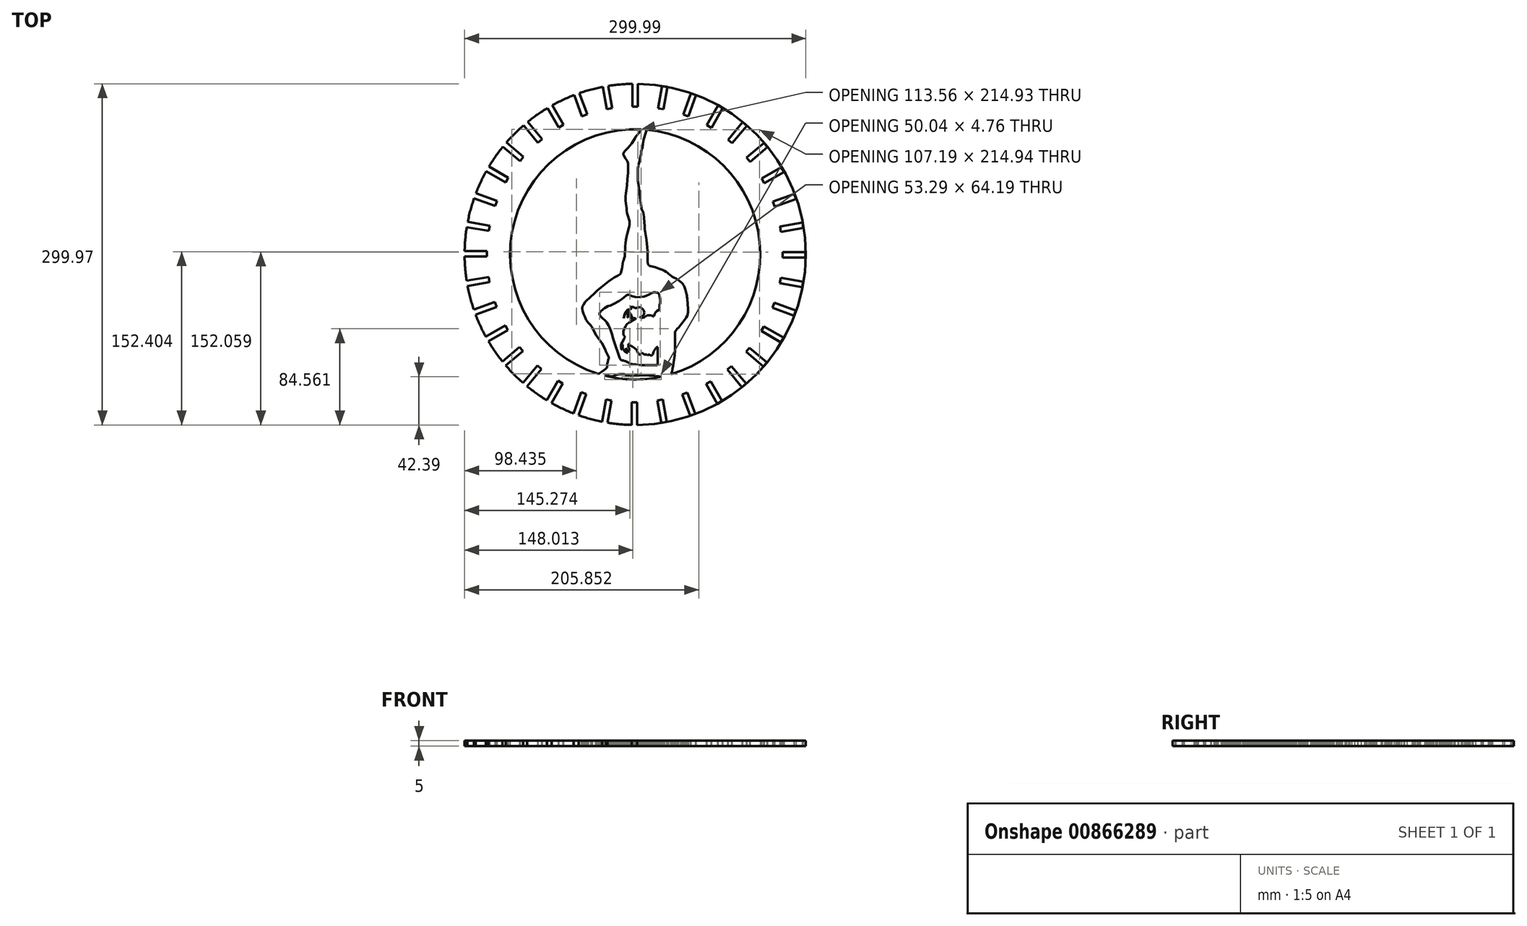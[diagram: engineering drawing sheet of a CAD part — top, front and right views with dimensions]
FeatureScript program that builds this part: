
annotation { "Feature Type Name" : "Feature", "Feature Type Description" : "" }
export const myFeature = defineFeature(function(context is Context, id is Id, definition is map)
    precondition{}
    {
        {
            var Q0;
            Q0=qCreatedBy(makeId("Top.planeOp"),FACE);
            var sketch = newSketch(context, id + "F0", { "sketchPlane" : qUnion([Q0])});
            skCircle(sketch, "E0", {"center": v(0, 0) * mm, "radius": 150 * mm});
            skLineSegment(sketch, "E1", {"start": v(0, 0) * mm, "end": v(0, 150) * mm});
            skPoint(sketch, "E2", {"position": v(0, 150) * mm});
            skPoint(sketch, "E3", {"position": v(0, 130) * mm});
            skLineSegment(sketch, "E4", {"start": v(-2.38, 130) * mm, "end": v(2.38, 130) * mm});
            skLineSegment(sketch, "E5", {"start": v(-2.38, 150) * mm, "end": v(2.37, 150) * mm});
            skLineSegment(sketch, "E6", {"start": v(-2.38, 150) * mm, "end": v(-2.38, 130) * mm});
            skLineSegment(sketch, "E7", {"start": v(2.38, 150) * mm, "end": v(2.38, 130) * mm});
            skCircle(sketch, "E8", {"center": v(0, 0) * mm, "radius": 110 * mm});
            skLineSegment(sketch, "E9.1.0", {"start": v(-28.4, 147.38) * mm, "end": v(-24.92, 127.68) * mm});
            skLineSegment(sketch, "E9.1.1", {"start": v(-23.71, 148.2) * mm, "end": v(-20.24, 128.5) * mm});
            skLineSegment(sketch, "E9.1.2", {"start": v(-28.4, 147.38) * mm, "end": v(-23.71, 148.2) * mm});
            skLineSegment(sketch, "E9.1.3", {"start": v(-24.92, 127.68) * mm, "end": v(-20.24, 128.5) * mm});
            skLineSegment(sketch, "E9.2.0", {"start": v(-53.56, 140.27) * mm, "end": v(-46.72, 121.48) * mm});
            skLineSegment(sketch, "E9.2.1", {"start": v(-49.1, 141.9) * mm, "end": v(-42.25, 123.1) * mm});
            skLineSegment(sketch, "E9.2.2", {"start": v(-53.56, 140.27) * mm, "end": v(-49.1, 141.9) * mm});
            skLineSegment(sketch, "E9.2.3", {"start": v(-46.72, 121.48) * mm, "end": v(-42.25, 123.1) * mm});
            skLineSegment(sketch, "E9.3.0", {"start": v(-77.1, 128.91) * mm, "end": v(-67.1, 111.6) * mm});
            skLineSegment(sketch, "E9.3.1", {"start": v(-73, 131.29) * mm, "end": v(-63, 113.97) * mm});
            skLineSegment(sketch, "E9.3.2", {"start": v(-77.1, 128.91) * mm, "end": v(-73, 131.29) * mm});
            skLineSegment(sketch, "E9.3.3", {"start": v(-67.1, 111.6) * mm, "end": v(-63, 113.97) * mm});
            skLineSegment(sketch, "E9.4.0", {"start": v(-98.33, 113.63) * mm, "end": v(-85.47, 98.3) * mm});
            skLineSegment(sketch, "E9.4.1", {"start": v(-94.69, 116.68) * mm, "end": v(-81.83, 101.36) * mm});
            skLineSegment(sketch, "E9.4.2", {"start": v(-98.33, 113.63) * mm, "end": v(-94.69, 116.68) * mm});
            skLineSegment(sketch, "E9.4.3", {"start": v(-85.47, 98.3) * mm, "end": v(-81.83, 101.36) * mm});
            skLineSegment(sketch, "E9.5.0", {"start": v(-116.57, 94.9) * mm, "end": v(-101.25, 82.04) * mm});
            skLineSegment(sketch, "E9.5.1", {"start": v(-113.52, 98.54) * mm, "end": v(-98.2, 85.68) * mm});
            skLineSegment(sketch, "E9.5.2", {"start": v(-116.57, 94.9) * mm, "end": v(-113.52, 98.54) * mm});
            skLineSegment(sketch, "E9.5.3", {"start": v(-101.25, 82.04) * mm, "end": v(-98.2, 85.68) * mm});
            skLineSegment(sketch, "E9.6.0", {"start": v(-131.29, 73.28) * mm, "end": v(-113.97, 63.28) * mm});
            skLineSegment(sketch, "E9.6.1", {"start": v(-128.91, 77.4) * mm, "end": v(-111.6, 67.4) * mm});
            skLineSegment(sketch, "E9.6.2", {"start": v(-131.29, 73.28) * mm, "end": v(-128.91, 77.4) * mm});
            skLineSegment(sketch, "E9.6.3", {"start": v(-113.97, 63.28) * mm, "end": v(-111.6, 67.4) * mm});
            skLineSegment(sketch, "E9.7.0", {"start": v(-142.02, 49.44) * mm, "end": v(-123.23, 42.6) * mm});
            skLineSegment(sketch, "E9.7.1", {"start": v(-140.4, 53.9) * mm, "end": v(-121.6, 47.06) * mm});
            skLineSegment(sketch, "E9.7.2", {"start": v(-142.02, 49.44) * mm, "end": v(-140.4, 53.9) * mm});
            skLineSegment(sketch, "E9.7.3", {"start": v(-123.23, 42.6) * mm, "end": v(-121.6, 47.06) * mm});
            skLineSegment(sketch, "E9.8.0", {"start": v(-148.45, 24.1) * mm, "end": v(-128.76, 20.62) * mm});
            skLineSegment(sketch, "E9.8.1", {"start": v(-147.63, 28.77) * mm, "end": v(-127.93, 25.3) * mm});
            skLineSegment(sketch, "E9.8.2", {"start": v(-148.45, 24.1) * mm, "end": v(-147.63, 28.77) * mm});
            skLineSegment(sketch, "E9.8.3", {"start": v(-128.76, 20.62) * mm, "end": v(-127.93, 25.3) * mm});
            skLineSegment(sketch, "E9.9.0", {"start": v(-150.39, -1.99) * mm, "end": v(-130.39, -1.99) * mm});
            skLineSegment(sketch, "E9.9.1", {"start": v(-150.39, 2.76) * mm, "end": v(-130.39, 2.76) * mm});
            skLineSegment(sketch, "E9.9.2", {"start": v(-150.39, -1.99) * mm, "end": v(-150.39, 2.76) * mm});
            skLineSegment(sketch, "E9.9.3", {"start": v(-130.39, -1.99) * mm, "end": v(-130.39, 2.76) * mm});
            skLineSegment(sketch, "E9.10.0", {"start": v(-147.77, -28) * mm, "end": v(-128.07, -24.53) * mm});
            skLineSegment(sketch, "E9.10.1", {"start": v(-148.59, -23.33) * mm, "end": v(-128.9, -19.85) * mm});
            skLineSegment(sketch, "E9.10.2", {"start": v(-147.77, -28) * mm, "end": v(-148.59, -23.33) * mm});
            skLineSegment(sketch, "E9.10.3", {"start": v(-128.07, -24.53) * mm, "end": v(-128.9, -19.85) * mm});
            skLineSegment(sketch, "E9.11.0", {"start": v(-140.66, -53.17) * mm, "end": v(-121.87, -46.33) * mm});
            skLineSegment(sketch, "E9.11.1", {"start": v(-142.29, -48.7) * mm, "end": v(-123.5, -41.87) * mm});
            skLineSegment(sketch, "E9.11.2", {"start": v(-140.66, -53.17) * mm, "end": v(-142.29, -48.7) * mm});
            skLineSegment(sketch, "E9.11.3", {"start": v(-121.87, -46.33) * mm, "end": v(-123.5, -41.87) * mm});
            skLineSegment(sketch, "E9.12.0", {"start": v(-129.3, -76.72) * mm, "end": v(-111.98, -66.72) * mm});
            skLineSegment(sketch, "E9.12.1", {"start": v(-131.67, -72.6) * mm, "end": v(-114.35, -62.6) * mm});
            skLineSegment(sketch, "E9.12.2", {"start": v(-129.3, -76.72) * mm, "end": v(-131.67, -72.6) * mm});
            skLineSegment(sketch, "E9.12.3", {"start": v(-111.98, -66.72) * mm, "end": v(-114.35, -62.6) * mm});
            skLineSegment(sketch, "E9.13.0", {"start": v(-114.02, -97.94) * mm, "end": v(-98.7, -85.08) * mm});
            skLineSegment(sketch, "E9.13.1", {"start": v(-117.07, -94.3) * mm, "end": v(-101.75, -81.45) * mm});
            skLineSegment(sketch, "E9.13.2", {"start": v(-114.02, -97.94) * mm, "end": v(-117.07, -94.3) * mm});
            skLineSegment(sketch, "E9.13.3", {"start": v(-98.7, -85.08) * mm, "end": v(-101.75, -81.45) * mm});
            skLineSegment(sketch, "E9.14.0", {"start": v(-95.29, -116.18) * mm, "end": v(-82.43, -100.86) * mm});
            skLineSegment(sketch, "E9.14.1", {"start": v(-98.92, -113.13) * mm, "end": v(-86.07, -97.8) * mm});
            skLineSegment(sketch, "E9.14.2", {"start": v(-95.29, -116.18) * mm, "end": v(-98.92, -113.13) * mm});
            skLineSegment(sketch, "E9.14.3", {"start": v(-82.43, -100.86) * mm, "end": v(-86.07, -97.8) * mm});
            skLineSegment(sketch, "E9.15.0", {"start": v(-73.67, -130.9) * mm, "end": v(-63.67, -113.58) * mm});
            skLineSegment(sketch, "E9.15.1", {"start": v(-77.78, -128.52) * mm, "end": v(-67.78, -111.2) * mm});
            skLineSegment(sketch, "E9.15.2", {"start": v(-73.67, -130.9) * mm, "end": v(-77.78, -128.52) * mm});
            skLineSegment(sketch, "E9.15.3", {"start": v(-63.67, -113.58) * mm, "end": v(-67.78, -111.2) * mm});
            skLineSegment(sketch, "E9.16.0", {"start": v(-49.83, -141.63) * mm, "end": v(-42.99, -122.84) * mm});
            skLineSegment(sketch, "E9.16.1", {"start": v(-54.29, -140) * mm, "end": v(-47.45, -121.21) * mm});
            skLineSegment(sketch, "E9.16.2", {"start": v(-49.83, -141.63) * mm, "end": v(-54.29, -140) * mm});
            skLineSegment(sketch, "E9.16.3", {"start": v(-42.99, -122.84) * mm, "end": v(-47.45, -121.21) * mm});
            skLineSegment(sketch, "E9.17.0", {"start": v(-24.48, -148.07) * mm, "end": v(-21, -128.37) * mm});
            skLineSegment(sketch, "E9.17.1", {"start": v(-29.16, -147.24) * mm, "end": v(-25.69, -127.55) * mm});
            skLineSegment(sketch, "E9.17.2", {"start": v(-24.48, -148.07) * mm, "end": v(-29.16, -147.24) * mm});
            skLineSegment(sketch, "E9.17.3", {"start": v(-21, -128.37) * mm, "end": v(-25.69, -127.55) * mm});
            skLineSegment(sketch, "E9.18.0", {"start": v(1.6, -150) * mm, "end": v(1.6, -130) * mm});
            skLineSegment(sketch, "E9.18.1", {"start": v(-3.15, -150) * mm, "end": v(-3.15, -130) * mm});
            skLineSegment(sketch, "E9.18.2", {"start": v(1.6, -150) * mm, "end": v(-3.15, -150) * mm});
            skLineSegment(sketch, "E9.18.3", {"start": v(1.6, -130) * mm, "end": v(-3.15, -130) * mm});
            skLineSegment(sketch, "E9.19.0", {"start": v(27.61, -147.38) * mm, "end": v(24.14, -127.68) * mm});
            skLineSegment(sketch, "E9.19.1", {"start": v(22.94, -148.2) * mm, "end": v(19.46, -128.5) * mm});
            skLineSegment(sketch, "E9.19.2", {"start": v(27.61, -147.38) * mm, "end": v(22.94, -148.2) * mm});
            skLineSegment(sketch, "E9.19.3", {"start": v(24.14, -127.68) * mm, "end": v(19.46, -128.5) * mm});
            skLineSegment(sketch, "E9.20.0", {"start": v(52.78, -140.27) * mm, "end": v(45.94, -121.48) * mm});
            skLineSegment(sketch, "E9.20.1", {"start": v(48.32, -141.9) * mm, "end": v(41.48, -123.1) * mm});
            skLineSegment(sketch, "E9.20.2", {"start": v(52.78, -140.27) * mm, "end": v(48.32, -141.9) * mm});
            skLineSegment(sketch, "E9.20.3", {"start": v(45.94, -121.48) * mm, "end": v(41.48, -123.1) * mm});
            skLineSegment(sketch, "E9.21.0", {"start": v(76.33, -128.91) * mm, "end": v(66.33, -111.6) * mm});
            skLineSegment(sketch, "E9.21.1", {"start": v(72.22, -131.29) * mm, "end": v(62.22, -113.97) * mm});
            skLineSegment(sketch, "E9.21.2", {"start": v(76.33, -128.91) * mm, "end": v(72.22, -131.29) * mm});
            skLineSegment(sketch, "E9.21.3", {"start": v(66.33, -111.6) * mm, "end": v(62.22, -113.97) * mm});
            skLineSegment(sketch, "E9.22.0", {"start": v(97.55, -113.63) * mm, "end": v(84.7, -98.3) * mm});
            skLineSegment(sketch, "E9.22.1", {"start": v(93.91, -116.68) * mm, "end": v(81.06, -101.36) * mm});
            skLineSegment(sketch, "E9.22.2", {"start": v(97.55, -113.63) * mm, "end": v(93.91, -116.68) * mm});
            skLineSegment(sketch, "E9.22.3", {"start": v(84.7, -98.3) * mm, "end": v(81.06, -101.36) * mm});
            skLineSegment(sketch, "E9.23.0", {"start": v(115.8, -94.9) * mm, "end": v(100.47, -82.04) * mm});
            skLineSegment(sketch, "E9.23.1", {"start": v(112.74, -98.54) * mm, "end": v(97.42, -85.68) * mm});
            skLineSegment(sketch, "E9.23.2", {"start": v(115.8, -94.9) * mm, "end": v(112.74, -98.54) * mm});
            skLineSegment(sketch, "E9.23.3", {"start": v(100.47, -82.04) * mm, "end": v(97.42, -85.68) * mm});
            skLineSegment(sketch, "E9.24.0", {"start": v(130.5, -73.28) * mm, "end": v(113.19, -63.28) * mm});
            skLineSegment(sketch, "E9.24.1", {"start": v(128.13, -77.4) * mm, "end": v(110.81, -67.4) * mm});
            skLineSegment(sketch, "E9.24.2", {"start": v(130.5, -73.28) * mm, "end": v(128.13, -77.4) * mm});
            skLineSegment(sketch, "E9.24.3", {"start": v(113.19, -63.28) * mm, "end": v(110.81, -67.4) * mm});
            skLineSegment(sketch, "E9.25.0", {"start": v(141.24, -49.44) * mm, "end": v(122.45, -42.6) * mm});
            skLineSegment(sketch, "E9.25.1", {"start": v(139.62, -53.9) * mm, "end": v(120.83, -47.06) * mm});
            skLineSegment(sketch, "E9.25.2", {"start": v(141.24, -49.44) * mm, "end": v(139.62, -53.9) * mm});
            skLineSegment(sketch, "E9.25.3", {"start": v(122.45, -42.6) * mm, "end": v(120.83, -47.06) * mm});
            skLineSegment(sketch, "E9.26.0", {"start": v(147.68, -24.1) * mm, "end": v(127.98, -20.62) * mm});
            skLineSegment(sketch, "E9.26.1", {"start": v(146.85, -28.77) * mm, "end": v(127.16, -25.3) * mm});
            skLineSegment(sketch, "E9.26.2", {"start": v(147.68, -24.1) * mm, "end": v(146.85, -28.77) * mm});
            skLineSegment(sketch, "E9.26.3", {"start": v(127.98, -20.62) * mm, "end": v(127.16, -25.3) * mm});
            skLineSegment(sketch, "E9.27.0", {"start": v(149.61, 1.99) * mm, "end": v(129.61, 1.99) * mm});
            skLineSegment(sketch, "E9.27.1", {"start": v(149.61, -2.76) * mm, "end": v(129.61, -2.76) * mm});
            skLineSegment(sketch, "E9.27.2", {"start": v(149.61, 1.99) * mm, "end": v(149.61, -2.76) * mm});
            skLineSegment(sketch, "E9.27.3", {"start": v(129.61, 1.99) * mm, "end": v(129.61, -2.76) * mm});
            skLineSegment(sketch, "E9.28.0", {"start": v(146.99, 28) * mm, "end": v(127.3, 24.53) * mm});
            skLineSegment(sketch, "E9.28.1", {"start": v(147.81, 23.33) * mm, "end": v(128.12, 19.85) * mm});
            skLineSegment(sketch, "E9.28.2", {"start": v(146.99, 28) * mm, "end": v(147.81, 23.33) * mm});
            skLineSegment(sketch, "E9.28.3", {"start": v(127.3, 24.53) * mm, "end": v(128.12, 19.85) * mm});
            skLineSegment(sketch, "E9.29.0", {"start": v(139.89, 53.17) * mm, "end": v(121.1, 46.33) * mm});
            skLineSegment(sketch, "E9.29.1", {"start": v(141.51, 48.7) * mm, "end": v(122.72, 41.87) * mm});
            skLineSegment(sketch, "E9.29.2", {"start": v(139.89, 53.17) * mm, "end": v(141.51, 48.7) * mm});
            skLineSegment(sketch, "E9.29.3", {"start": v(121.1, 46.33) * mm, "end": v(122.72, 41.87) * mm});
            skLineSegment(sketch, "E9.30.0", {"start": v(128.52, 76.72) * mm, "end": v(111.2, 66.72) * mm});
            skLineSegment(sketch, "E9.30.1", {"start": v(130.9, 72.6) * mm, "end": v(113.58, 62.6) * mm});
            skLineSegment(sketch, "E9.30.2", {"start": v(128.52, 76.72) * mm, "end": v(130.9, 72.6) * mm});
            skLineSegment(sketch, "E9.30.3", {"start": v(111.2, 66.72) * mm, "end": v(113.58, 62.6) * mm});
            skLineSegment(sketch, "E9.31.0", {"start": v(113.24, 97.94) * mm, "end": v(97.92, 85.08) * mm});
            skLineSegment(sketch, "E9.31.1", {"start": v(116.3, 94.3) * mm, "end": v(100.97, 81.45) * mm});
            skLineSegment(sketch, "E9.31.2", {"start": v(113.24, 97.94) * mm, "end": v(116.3, 94.3) * mm});
            skLineSegment(sketch, "E9.31.3", {"start": v(97.92, 85.08) * mm, "end": v(100.97, 81.45) * mm});
            skLineSegment(sketch, "E9.32.0", {"start": v(94.5, 116.18) * mm, "end": v(81.65, 100.86) * mm});
            skLineSegment(sketch, "E9.32.1", {"start": v(98.15, 113.13) * mm, "end": v(85.3, 97.8) * mm});
            skLineSegment(sketch, "E9.32.2", {"start": v(94.5, 116.18) * mm, "end": v(98.15, 113.13) * mm});
            skLineSegment(sketch, "E9.32.3", {"start": v(81.65, 100.86) * mm, "end": v(85.3, 97.8) * mm});
            skLineSegment(sketch, "E9.33.0", {"start": v(72.9, 130.9) * mm, "end": v(62.9, 113.58) * mm});
            skLineSegment(sketch, "E9.33.1", {"start": v(77, 128.52) * mm, "end": v(67, 111.2) * mm});
            skLineSegment(sketch, "E9.33.2", {"start": v(72.9, 130.9) * mm, "end": v(77, 128.52) * mm});
            skLineSegment(sketch, "E9.33.3", {"start": v(62.9, 113.58) * mm, "end": v(67, 111.2) * mm});
            skLineSegment(sketch, "E9.34.0", {"start": v(49.05, 141.63) * mm, "end": v(42.2, 122.84) * mm});
            skLineSegment(sketch, "E9.34.1", {"start": v(53.51, 140) * mm, "end": v(46.67, 121.21) * mm});
            skLineSegment(sketch, "E9.34.2", {"start": v(49.05, 141.63) * mm, "end": v(53.51, 140) * mm});
            skLineSegment(sketch, "E9.34.3", {"start": v(42.2, 122.84) * mm, "end": v(46.67, 121.21) * mm});
            skLineSegment(sketch, "E9.35.0", {"start": v(23.7, 148.07) * mm, "end": v(20.23, 128.37) * mm});
            skLineSegment(sketch, "E9.35.1", {"start": v(28.38, 147.24) * mm, "end": v(24.9, 127.55) * mm});
            skLineSegment(sketch, "E9.35.2", {"start": v(23.7, 148.07) * mm, "end": v(28.38, 147.24) * mm});
            skLineSegment(sketch, "E9.35.3", {"start": v(20.23, 128.37) * mm, "end": v(24.9, 127.55) * mm});
            skPoint(sketch, "E9.center", {"position": v(-0.39, 0) * mm});
            skSolve(sketch);
        }
        {
            var Q0;
            Q0=makeQuery(id+"F0.imprint","IMPRINT",FACE,{"disambiguationData":[TD([[makeQuery(id+"F0.imprint","IMPRINT",EDGE,{"derivedFrom":sQuery(id+"F0.wireOp",EDGE,"E8")}),-1.0]])]});
            extrude(context, id + "F1", {"entities" : qUnion([Q0]), "depth" : 5 * mm, "offsetDistance" : 25 * mm});
        }
        {
            var Q0;
            Q0=qCreatedBy(makeId("Top.planeOp"),FACE);
            var sketch = newSketch(context, id + "F2", { "sketchPlane" : qUnion([Q0])});
            skLineSegment(sketch, "E10", {"start": v(6.83, 111.87) * mm, "end": v(5.33, 110.02) * mm});
            skLineSegment(sketch, "E11", {"start": v(5.33, 110.02) * mm, "end": v(4.16, 108.4) * mm});
            skLineSegment(sketch, "E12", {"start": v(4.16, 108.4) * mm, "end": v(3.77, 107.3) * mm});
            skLineSegment(sketch, "E13", {"start": v(3.77, 107.3) * mm, "end": v(3.08, 106.38) * mm});
            skLineSegment(sketch, "E14", {"start": v(3.08, 106.38) * mm, "end": v(1.66, 104.89) * mm});
            skLineSegment(sketch, "E15", {"start": v(1.66, 104.89) * mm, "end": v(0.57, 103.56) * mm});
            skLineSegment(sketch, "E16", {"start": v(0.57, 103.56) * mm, "end": v(-0.34, 102.02) * mm});
            skLineSegment(sketch, "E17", {"start": v(-0.34, 102.02) * mm, "end": v(-1.86, 99.5) * mm});
            skLineSegment(sketch, "E18", {"start": v(-1.86, 99.5) * mm, "end": v(-3.07, 97.48) * mm});
            skLineSegment(sketch, "E19", {"start": v(-3.07, 97.48) * mm, "end": v(-4.65, 95.48) * mm});
            skLineSegment(sketch, "E20", {"start": v(-4.65, 95.48) * mm, "end": v(-6.3, 93.59) * mm});
            skLineSegment(sketch, "E21", {"start": v(-6.3, 93.59) * mm, "end": v(-7.83, 92.24) * mm});
            skLineSegment(sketch, "E22", {"start": v(-7.83, 92.24) * mm, "end": v(-8.94, 91.04) * mm});
            skLineSegment(sketch, "E23", {"start": v(-8.94, 91.04) * mm, "end": v(-9.48, 90.42) * mm});
            skLineSegment(sketch, "E24", {"start": v(-9.48, 90.42) * mm, "end": v(-10.02, 89.32) * mm});
            skLineSegment(sketch, "E25", {"start": v(-10.02, 89.32) * mm, "end": v(-10.24, 88.58) * mm});
            skLineSegment(sketch, "E26", {"start": v(-10.24, 88.58) * mm, "end": v(-10.37, 87.93) * mm});
            skLineSegment(sketch, "E27", {"start": v(-10.37, 87.93) * mm, "end": v(-10.37, 87.56) * mm});
            skLineSegment(sketch, "E28", {"start": v(-10.37, 87.56) * mm, "end": v(-9.88, 86.5) * mm});
            skLineSegment(sketch, "E29", {"start": v(-9.88, 86.5) * mm, "end": v(-9.17, 85.4) * mm});
            skLineSegment(sketch, "E30", {"start": v(-9.17, 85.4) * mm, "end": v(-8.4, 84.2) * mm});
            skLineSegment(sketch, "E31", {"start": v(-8.4, 84.2) * mm, "end": v(-7.39, 82.8) * mm});
            skLineSegment(sketch, "E32", {"start": v(-7.39, 82.8) * mm, "end": v(-6.91, 82.05) * mm});
            skLineSegment(sketch, "E33", {"start": v(-6.91, 82.05) * mm, "end": v(-6.5, 81.01) * mm});
            skLineSegment(sketch, "E34", {"start": v(-6.5, 81.01) * mm, "end": v(-6.3, 79.61) * mm});
            skLineSegment(sketch, "E35", {"start": v(-6.3, 79.61) * mm, "end": v(-6.2, 78.09) * mm});
            skLineSegment(sketch, "E36", {"start": v(-6.2, 78.09) * mm, "end": v(-6.28, 74.36) * mm});
            skLineSegment(sketch, "E37", {"start": v(-6.28, 74.36) * mm, "end": v(-6.4, 71.72) * mm});
            skLineSegment(sketch, "E38", {"start": v(-6.4, 71.72) * mm, "end": v(-6.74, 66.24) * mm});
            skLineSegment(sketch, "E39", {"start": v(-6.74, 66.24) * mm, "end": v(-7.25, 60.37) * mm});
            skLineSegment(sketch, "E40", {"start": v(-7.25, 60.37) * mm, "end": v(-8.18, 53.6) * mm});
            skLineSegment(sketch, "E41", {"start": v(-8.18, 53.6) * mm, "end": v(-8.44, 51.24) * mm});
            skLineSegment(sketch, "E42", {"start": v(-8.44, 51.24) * mm, "end": v(-8.5, 49.8) * mm});
            skLineSegment(sketch, "E43", {"start": v(-8.5, 49.8) * mm, "end": v(-8.34, 47.26) * mm});
            skLineSegment(sketch, "E44", {"start": v(-8.34, 47.26) * mm, "end": v(-8.04, 44.53) * mm});
            skLineSegment(sketch, "E45", {"start": v(-8.04, 44.53) * mm, "end": v(-7.56, 40.85) * mm});
            skLineSegment(sketch, "E46", {"start": v(-7.56, 40.85) * mm, "end": v(-7.37, 38.85) * mm});
            skLineSegment(sketch, "E47", {"start": v(-7.37, 38.85) * mm, "end": v(-7.07, 36.3) * mm});
            skLineSegment(sketch, "E48", {"start": v(-7.07, 36.3) * mm, "end": v(-6.66, 34.38) * mm});
            skLineSegment(sketch, "E49", {"start": v(-6.66, 34.38) * mm, "end": v(-5.65, 31.06) * mm});
            skLineSegment(sketch, "E50", {"start": v(-5.65, 31.06) * mm, "end": v(-5.3, 29.94) * mm});
            skLineSegment(sketch, "E51", {"start": v(-5.3, 29.94) * mm, "end": v(-5.12, 29.34) * mm});
            skLineSegment(sketch, "E52", {"start": v(-5.12, 29.34) * mm, "end": v(-4.98, 28.57) * mm});
            skLineSegment(sketch, "E53", {"start": v(-4.98, 28.57) * mm, "end": v(-4.91, 28) * mm});
            skLineSegment(sketch, "E54", {"start": v(-4.91, 28) * mm, "end": v(-4.91, 27.25) * mm});
            skLineSegment(sketch, "E55", {"start": v(-4.91, 27.25) * mm, "end": v(-5, 26.34) * mm});
            skLineSegment(sketch, "E56", {"start": v(-5, 26.34) * mm, "end": v(-5.41, 24.2) * mm});
            skLineSegment(sketch, "E57", {"start": v(-5.41, 24.2) * mm, "end": v(-5.59, 23.26) * mm});
            skLineSegment(sketch, "E58", {"start": v(-5.59, 23.26) * mm, "end": v(-6.96, 18.4) * mm});
            skLineSegment(sketch, "E59", {"start": v(-6.96, 18.4) * mm, "end": v(-7.52, 15.81) * mm});
            skLineSegment(sketch, "E60", {"start": v(-7.52, 15.81) * mm, "end": v(-8.04, 12.8) * mm});
            skLineSegment(sketch, "E61", {"start": v(-8.04, 12.8) * mm, "end": v(-8.43, 9.95) * mm});
            skLineSegment(sketch, "E62", {"start": v(-8.43, 9.95) * mm, "end": v(-8.64, 7.37) * mm});
            skLineSegment(sketch, "E63", {"start": v(-8.64, 7.37) * mm, "end": v(-8.9, 4.72) * mm});
            skLineSegment(sketch, "E64", {"start": v(-8.9, 4.72) * mm, "end": v(-9.08, 1.36) * mm});
            skLineSegment(sketch, "E65", {"start": v(-9.08, 1.36) * mm, "end": v(-9.08, -0.48) * mm});
            skLineSegment(sketch, "E66", {"start": v(-9.08, -0.48) * mm, "end": v(-9.08, -0.93) * mm});
            skLineSegment(sketch, "E67", {"start": v(-9.08, -0.93) * mm, "end": v(-9.18, -1.73) * mm});
            skLineSegment(sketch, "E68", {"start": v(-9.18, -1.73) * mm, "end": v(-9.63, -3.56) * mm});
            skLineSegment(sketch, "E69", {"start": v(-9.63, -3.56) * mm, "end": v(-10.14, -5) * mm});
            skLineSegment(sketch, "E70", {"start": v(-10.14, -5) * mm, "end": v(-10.54, -6.3) * mm});
            skLineSegment(sketch, "E71", {"start": v(-10.54, -6.3) * mm, "end": v(-11, -8.25) * mm});
            skLineSegment(sketch, "E72", {"start": v(-11, -8.25) * mm, "end": v(-11.46, -10.75) * mm});
            skLineSegment(sketch, "E73", {"start": v(-11.46, -10.75) * mm, "end": v(-11.77, -12.7) * mm});
            skLineSegment(sketch, "E74", {"start": v(-11.77, -12.7) * mm, "end": v(-12.11, -14.95) * mm});
            skLineSegment(sketch, "E75", {"start": v(-12.11, -14.95) * mm, "end": v(-12.45, -16.37) * mm});
            skLineSegment(sketch, "E76", {"start": v(-12.45, -16.37) * mm, "end": v(-12.62, -16.65) * mm});
            skLineSegment(sketch, "E77", {"start": v(-12.62, -16.65) * mm, "end": v(-12.95, -17.06) * mm});
            skLineSegment(sketch, "E78", {"start": v(-12.95, -17.06) * mm, "end": v(-13.17, -17.3) * mm});
            skLineSegment(sketch, "E79", {"start": v(-13.17, -17.3) * mm, "end": v(-15.1, -18.65) * mm});
            skLineSegment(sketch, "E80", {"start": v(-15.1, -18.65) * mm, "end": v(-18.23, -20.4) * mm});
            skLineSegment(sketch, "E81", {"start": v(-18.23, -20.4) * mm, "end": v(-20.15, -21.5) * mm});
            skLineSegment(sketch, "E82", {"start": v(-20.15, -21.5) * mm, "end": v(-23.4, -23.82) * mm});
            skLineSegment(sketch, "E83", {"start": v(-23.4, -23.82) * mm, "end": v(-26.73, -26.25) * mm});
            skLineSegment(sketch, "E84", {"start": v(-26.73, -26.25) * mm, "end": v(-29.8, -28.68) * mm});
            skLineSegment(sketch, "E85", {"start": v(-29.8, -28.68) * mm, "end": v(-33.17, -31.63) * mm});
            skLineSegment(sketch, "E86", {"start": v(-33.17, -31.63) * mm, "end": v(-36.23, -34.54) * mm});
            skLineSegment(sketch, "E87", {"start": v(-36.23, -34.54) * mm, "end": v(-39.37, -37.52) * mm});
            skLineSegment(sketch, "E88", {"start": v(-39.37, -37.52) * mm, "end": v(-42.95, -40.84) * mm});
            skLineSegment(sketch, "E89", {"start": v(-42.95, -40.84) * mm, "end": v(-43.82, -41.65) * mm});
            skLineSegment(sketch, "E90", {"start": v(-43.82, -41.65) * mm, "end": v(-44.03, -41.92) * mm});
            skLineSegment(sketch, "E91", {"start": v(-44.03, -41.92) * mm, "end": v(-44.92, -43.25) * mm});
            skLineSegment(sketch, "E92", {"start": v(-44.92, -43.25) * mm, "end": v(-45.46, -44.05) * mm});
            skLineSegment(sketch, "E93", {"start": v(-45.46, -44.05) * mm, "end": v(-45.77, -44.68) * mm});
            skLineSegment(sketch, "E94", {"start": v(-45.77, -44.68) * mm, "end": v(-46.1, -45.47) * mm});
            skLineSegment(sketch, "E95", {"start": v(-46.1, -45.47) * mm, "end": v(-46.27, -46) * mm});
            skLineSegment(sketch, "E96", {"start": v(-46.27, -46) * mm, "end": v(-46.4, -46.58) * mm});
            skLineSegment(sketch, "E97", {"start": v(-46.4, -46.58) * mm, "end": v(-46.48, -47.02) * mm});
            skLineSegment(sketch, "E98", {"start": v(-46.48, -47.02) * mm, "end": v(-46.53, -47.45) * mm});
            skLineSegment(sketch, "E99", {"start": v(-46.53, -47.45) * mm, "end": v(-46.55, -47.72) * mm});
            skLineSegment(sketch, "E100", {"start": v(-46.55, -47.72) * mm, "end": v(-46.54, -48.18) * mm});
            skLineSegment(sketch, "E101", {"start": v(-46.54, -48.18) * mm, "end": v(-46.4, -48.54) * mm});
            skLineSegment(sketch, "E102", {"start": v(-46.4, -48.54) * mm, "end": v(-46.32, -48.82) * mm});
            skLineSegment(sketch, "E103", {"start": v(-46.32, -48.82) * mm, "end": v(-46.22, -49.85) * mm});
            skLineSegment(sketch, "E104", {"start": v(-46.22, -49.85) * mm, "end": v(-46, -50.79) * mm});
            skLineSegment(sketch, "E105", {"start": v(-46, -50.79) * mm, "end": v(-45.26, -52.58) * mm});
            skLineSegment(sketch, "E106", {"start": v(-45.26, -52.58) * mm, "end": v(-44.28, -54.67) * mm});
            skLineSegment(sketch, "E107", {"start": v(-44.28, -54.67) * mm, "end": v(-43.34, -56.95) * mm});
            skLineSegment(sketch, "E108", {"start": v(-43.34, -56.95) * mm, "end": v(-43.06, -57.6) * mm});
            skLineSegment(sketch, "E109", {"start": v(-43.06, -57.6) * mm, "end": v(-42.4, -58.69) * mm});
            skLineSegment(sketch, "E110", {"start": v(-42.4, -58.69) * mm, "end": v(-41.05, -60.29) * mm});
            skLineSegment(sketch, "E111", {"start": v(-41.05, -60.29) * mm, "end": v(-40, -61.41) * mm});
            skLineSegment(sketch, "E112", {"start": v(-40, -61.41) * mm, "end": v(-39.2, -62.28) * mm});
            skLineSegment(sketch, "E113", {"start": v(-39.2, -62.28) * mm, "end": v(-38.64, -63.07) * mm});
            skLineSegment(sketch, "E114", {"start": v(-38.64, -63.07) * mm, "end": v(-37.84, -64.45) * mm});
            skLineSegment(sketch, "E115", {"start": v(-37.84, -64.45) * mm, "end": v(-36.99, -66.04) * mm});
            skLineSegment(sketch, "E116", {"start": v(-36.99, -66.04) * mm, "end": v(-36.03, -67.87) * mm});
            skLineSegment(sketch, "E117", {"start": v(-36.03, -67.87) * mm, "end": v(-35.19, -69.45) * mm});
            skLineSegment(sketch, "E118", {"start": v(-35.19, -69.45) * mm, "end": v(-34.36, -70.9) * mm});
            skLineSegment(sketch, "E119", {"start": v(-34.36, -70.9) * mm, "end": v(-33.82, -71.78) * mm});
            skLineSegment(sketch, "E120", {"start": v(-33.82, -71.78) * mm, "end": v(-32.49, -73.57) * mm});
            skLineSegment(sketch, "E121", {"start": v(-32.49, -73.57) * mm, "end": v(-31.58, -74.76) * mm});
            skLineSegment(sketch, "E122", {"start": v(-31.58, -74.76) * mm, "end": v(-31.28, -75.2) * mm});
            skLineSegment(sketch, "E123", {"start": v(-31.28, -75.2) * mm, "end": v(-30.68, -76.05) * mm});
            skLineSegment(sketch, "E124", {"start": v(-30.68, -76.05) * mm, "end": v(-29.53, -77.82) * mm});
            skLineSegment(sketch, "E125", {"start": v(-29.53, -77.82) * mm, "end": v(-28.26, -80.02) * mm});
            skLineSegment(sketch, "E126", {"start": v(-28.26, -80.02) * mm, "end": v(-27.46, -81.54) * mm});
            skLineSegment(sketch, "E127", {"start": v(-27.46, -81.54) * mm, "end": v(-26.17, -84) * mm});
            skLineSegment(sketch, "E128", {"start": v(-26.17, -84) * mm, "end": v(-25.83, -84.73) * mm});
            skLineSegment(sketch, "E129", {"start": v(-25.83, -84.73) * mm, "end": v(-25.77, -84.93) * mm});
            skLineSegment(sketch, "E130", {"start": v(-25.77, -84.93) * mm, "end": v(-24.35, -88.07) * mm});
            skLineSegment(sketch, "E131", {"start": v(-24.35, -88.07) * mm, "end": v(-23.47, -89.97) * mm});
            skLineSegment(sketch, "E132", {"start": v(-23.47, -89.97) * mm, "end": v(-23.27, -90.4) * mm});
            skLineSegment(sketch, "E133", {"start": v(-23.27, -90.4) * mm, "end": v(-23.23, -90.56) * mm});
            skLineSegment(sketch, "E134", {"start": v(-23.23, -90.56) * mm, "end": v(-23.19, -90.82) * mm});
            skLineSegment(sketch, "E135", {"start": v(-23.19, -90.82) * mm, "end": v(-23.19, -91.25) * mm});
            skLineSegment(sketch, "E136", {"start": v(-23.19, -91.25) * mm, "end": v(-23.3, -91.85) * mm});
            skLineSegment(sketch, "E137", {"start": v(-23.3, -91.85) * mm, "end": v(-23.57, -92.63) * mm});
            skLineSegment(sketch, "E138", {"start": v(-23.57, -92.63) * mm, "end": v(-23.84, -93.2) * mm});
            skLineSegment(sketch, "E139", {"start": v(-23.84, -93.2) * mm, "end": v(-23.98, -93.71) * mm});
            skLineSegment(sketch, "E140", {"start": v(-23.98, -93.71) * mm, "end": v(-24.13, -94.4) * mm});
            skLineSegment(sketch, "E141", {"start": v(-24.13, -94.4) * mm, "end": v(-24.3, -95.05) * mm});
            skLineSegment(sketch, "E142", {"start": v(-24.3, -95.05) * mm, "end": v(-24.46, -95.78) * mm});
            skLineSegment(sketch, "E143", {"start": v(-24.46, -95.78) * mm, "end": v(-24.58, -96.36) * mm});
            skLineSegment(sketch, "E144", {"start": v(-24.58, -96.36) * mm, "end": v(-24.65, -96.86) * mm});
            skLineSegment(sketch, "E145", {"start": v(-24.65, -96.86) * mm, "end": v(-24.68, -97.12) * mm});
            skLineSegment(sketch, "E146", {"start": v(-24.68, -97.12) * mm, "end": v(-24.68, -97.53) * mm});
            skLineSegment(sketch, "E147", {"start": v(-24.68, -97.53) * mm, "end": v(-24.6, -98.08) * mm});
            skLineSegment(sketch, "E148", {"start": v(-24.6, -98.08) * mm, "end": v(-24.58, -98.59) * mm});
            skLineSegment(sketch, "E149", {"start": v(-24.58, -98.59) * mm, "end": v(-24.58, -98.93) * mm});
            skLineSegment(sketch, "E150", {"start": v(-24.58, -98.93) * mm, "end": v(-24.61, -99.09) * mm});
            skLineSegment(sketch, "E151", {"start": v(-24.61, -99.09) * mm, "end": v(-24.8, -99.39) * mm});
            skLineSegment(sketch, "E152", {"start": v(-24.8, -99.39) * mm, "end": v(-25.08, -99.76) * mm});
            skLineSegment(sketch, "E153", {"start": v(-25.08, -99.76) * mm, "end": v(-25.42, -100.08) * mm});
            skLineSegment(sketch, "E154", {"start": v(-25.42, -100.08) * mm, "end": v(-26.37, -100.97) * mm});
            skLineSegment(sketch, "E155", {"start": v(-26.37, -100.97) * mm, "end": v(-27.57, -101.89) * mm});
            skLineSegment(sketch, "E156", {"start": v(-27.57, -101.89) * mm, "end": v(-29.77, -103.38) * mm});
            skLineSegment(sketch, "E157", {"start": v(-29.77, -103.38) * mm, "end": v(-31.64, -104.6) * mm});
            skLineSegment(sketch, "E158", {"start": v(-31.64, -104.6) * mm, "end": v(-32.04, -104.78) * mm});
            skLineSegment(sketch, "E159", {"start": v(-32.04, -104.78) * mm, "end": v(-32.66, -105.06) * mm});
            skLineSegment(sketch, "E160", {"start": v(-32.66, -105.06) * mm, "end": v(-33.66, -105.37) * mm});
            skLineSegment(sketch, "E161", {"start": v(-33.66, -105.37) * mm, "end": v(-34.75, -105.7) * mm});
            skLineSegment(sketch, "E162", {"start": v(-34.75, -105.7) * mm, "end": v(-35.27, -105.86) * mm});
            skLineSegment(sketch, "E163", {"start": v(-35.27, -105.86) * mm, "end": v(-35.72, -106) * mm});
            skLineSegment(sketch, "E164", {"start": v(-35.72, -106) * mm, "end": v(-36.2, -106.07) * mm});
            skLineSegment(sketch, "E165", {"start": v(-36.2, -106.07) * mm, "end": v(-36.59, -106.18) * mm});
            skLineSegment(sketch, "E166", {"start": v(-36.59, -106.18) * mm, "end": v(-36.77, -106.27) * mm});
            skLineSegment(sketch, "E167", {"start": v(-36.77, -106.27) * mm, "end": v(-36.82, -106.35) * mm});
            skLineSegment(sketch, "E168", {"start": v(-36.82, -106.35) * mm, "end": v(-36.85, -106.5) * mm});
            skLineSegment(sketch, "E169", {"start": v(-36.85, -106.5) * mm, "end": v(-36.8, -106.67) * mm});
            skLineSegment(sketch, "E170", {"start": v(-36.8, -106.67) * mm, "end": v(-36.67, -106.86) * mm});
            skLineSegment(sketch, "E171", {"start": v(-36.67, -106.86) * mm, "end": v(-36.46, -107.02) * mm});
            skLineSegment(sketch, "E172", {"start": v(-36.46, -107.02) * mm, "end": v(-36.31, -107.07) * mm});
            skLineSegment(sketch, "E173", {"start": v(-36.31, -107.07) * mm, "end": v(-36.19, -107.1) * mm});
            skLineSegment(sketch, "E174", {"start": v(-36.19, -107.1) * mm, "end": v(-32.78, -107.1) * mm});
            skLineSegment(sketch, "E175", {"start": v(-32.78, -107.1) * mm, "end": v(-31.03, -107.1) * mm});
            skLineSegment(sketch, "E176", {"start": v(-31.03, -107.1) * mm, "end": v(-30.82, -107.06) * mm});
            skLineSegment(sketch, "E177", {"start": v(-30.82, -107.06) * mm, "end": v(-30.43, -107) * mm});
            skLineSegment(sketch, "E178", {"start": v(-30.43, -107) * mm, "end": v(-30.06, -106.95) * mm});
            skLineSegment(sketch, "E179", {"start": v(-30.06, -106.95) * mm, "end": v(-29.54, -106.87) * mm});
            skLineSegment(sketch, "E180", {"start": v(-29.54, -106.87) * mm, "end": v(-29.47, -106.86) * mm});
            skLineSegment(sketch, "E181", {"start": v(-29.47, -106.86) * mm, "end": v(-29.23, -106.86) * mm});
            skLineSegment(sketch, "E182", {"start": v(-29.23, -106.86) * mm, "end": v(-28.9, -106.86) * mm});
            skLineSegment(sketch, "E183", {"start": v(-28.9, -106.86) * mm, "end": v(-28.3, -106.83) * mm});
            skLineSegment(sketch, "E184", {"start": v(-28.3, -106.83) * mm, "end": v(-28.03, -106.74) * mm});
            skLineSegment(sketch, "E185", {"start": v(-28.03, -106.74) * mm, "end": v(-27.64, -106.69) * mm});
            skLineSegment(sketch, "E186", {"start": v(-27.64, -106.69) * mm, "end": v(-26.96, -106.63) * mm});
            skLineSegment(sketch, "E187", {"start": v(-26.96, -106.63) * mm, "end": v(-26.51, -106.6) * mm});
            skLineSegment(sketch, "E188", {"start": v(-26.51, -106.6) * mm, "end": v(-26.23, -106.57) * mm});
            skLineSegment(sketch, "E189", {"start": v(-26.23, -106.57) * mm, "end": v(-25.95, -106.55) * mm});
            skLineSegment(sketch, "E190", {"start": v(-25.95, -106.55) * mm, "end": v(-25.7, -106.55) * mm});
            skLineSegment(sketch, "E191", {"start": v(-25.7, -106.55) * mm, "end": v(-25.33, -106.57) * mm});
            skLineSegment(sketch, "E192", {"start": v(-25.33, -106.57) * mm, "end": v(-24.74, -106.63) * mm});
            skLineSegment(sketch, "E193", {"start": v(-24.74, -106.63) * mm, "end": v(-24.06, -106.77) * mm});
            skLineSegment(sketch, "E194", {"start": v(-24.06, -106.77) * mm, "end": v(-23.53, -106.95) * mm});
            skLineSegment(sketch, "E195", {"start": v(-23.53, -106.95) * mm, "end": v(-23.19, -107.07) * mm});
            skLineSegment(sketch, "E196", {"start": v(-23.19, -107.07) * mm, "end": v(-22.54, -107.2) * mm});
            skLineSegment(sketch, "E197", {"start": v(-22.54, -107.2) * mm, "end": v(-22.07, -107.3) * mm});
            skLineSegment(sketch, "E198", {"start": v(-22.07, -107.3) * mm, "end": v(-21.23, -107.3) * mm});
            skLineSegment(sketch, "E199", {"start": v(-21.23, -107.3) * mm, "end": v(-20.48, -107.3) * mm});
            skLineSegment(sketch, "E200", {"start": v(-20.48, -107.3) * mm, "end": v(-20.06, -107.27) * mm});
            skLineSegment(sketch, "E201", {"start": v(-20.06, -107.27) * mm, "end": v(-19.74, -107.17) * mm});
            skLineSegment(sketch, "E202", {"start": v(-19.74, -107.17) * mm, "end": v(-19.26, -107.1) * mm});
            skLineSegment(sketch, "E203", {"start": v(-19.26, -107.1) * mm, "end": v(-19.02, -107.02) * mm});
            skLineSegment(sketch, "E204", {"start": v(-19.02, -107.02) * mm, "end": v(-18.3, -106.74) * mm});
            skLineSegment(sketch, "E205", {"start": v(-18.3, -106.74) * mm, "end": v(-17.46, -106.38) * mm});
            skLineSegment(sketch, "E206", {"start": v(-17.46, -106.38) * mm, "end": v(-16.84, -106.1) * mm});
            skLineSegment(sketch, "E207", {"start": v(-16.84, -106.1) * mm, "end": v(-16.35, -105.87) * mm});
            skLineSegment(sketch, "E208", {"start": v(-16.35, -105.87) * mm, "end": v(-15.79, -105.7) * mm});
            skLineSegment(sketch, "E209", {"start": v(-15.79, -105.7) * mm, "end": v(-15.1, -105.53) * mm});
            skLineSegment(sketch, "E210", {"start": v(-15.1, -105.53) * mm, "end": v(-14.59, -105.45) * mm});
            skLineSegment(sketch, "E211", {"start": v(-14.59, -105.45) * mm, "end": v(-13.86, -105.45) * mm});
            skLineSegment(sketch, "E212", {"start": v(-13.86, -105.45) * mm, "end": v(-13.3, -105.37) * mm});
            skLineSegment(sketch, "E213", {"start": v(-13.3, -105.37) * mm, "end": v(-12.8, -105.3) * mm});
            skLineSegment(sketch, "E214", {"start": v(-12.8, -105.3) * mm, "end": v(-12.17, -105.25) * mm});
            skLineSegment(sketch, "E215", {"start": v(-12.17, -105.25) * mm, "end": v(-11.73, -105.25) * mm});
            skLineSegment(sketch, "E216", {"start": v(-11.73, -105.25) * mm, "end": v(-11.26, -105.22) * mm});
            skLineSegment(sketch, "E217", {"start": v(-11.26, -105.22) * mm, "end": v(-10.76, -105.22) * mm});
            skLineSegment(sketch, "E218", {"start": v(-10.76, -105.22) * mm, "end": v(-10.4, -105.22) * mm});
            skLineSegment(sketch, "E219", {"start": v(-10.4, -105.22) * mm, "end": v(-10.1, -105.25) * mm});
            skLineSegment(sketch, "E220", {"start": v(-10.1, -105.25) * mm, "end": v(-9.85, -105.36) * mm});
            skLineSegment(sketch, "E221", {"start": v(-9.85, -105.36) * mm, "end": v(-9.64, -105.44) * mm});
            skLineSegment(sketch, "E222", {"start": v(-9.64, -105.44) * mm, "end": v(-8.89, -105.62) * mm});
            skLineSegment(sketch, "E223", {"start": v(-8.89, -105.62) * mm, "end": v(-8.27, -105.83) * mm});
            skLineSegment(sketch, "E224", {"start": v(-8.27, -105.83) * mm, "end": v(-7.57, -106.1) * mm});
            skLineSegment(sketch, "E225", {"start": v(-7.57, -106.1) * mm, "end": v(-6.85, -106.38) * mm});
            skLineSegment(sketch, "E226", {"start": v(-6.85, -106.38) * mm, "end": v(-5.66, -106.79) * mm});
            skLineSegment(sketch, "E227", {"start": v(-5.66, -106.79) * mm, "end": v(-5.18, -106.95) * mm});
            skLineSegment(sketch, "E228", {"start": v(-5.18, -106.95) * mm, "end": v(-4.74, -107.04) * mm});
            skLineSegment(sketch, "E229", {"start": v(-4.74, -107.04) * mm, "end": v(-4.16, -107.1) * mm});
            skLineSegment(sketch, "E230", {"start": v(-4.16, -107.1) * mm, "end": v(-3.5, -107.1) * mm});
            skLineSegment(sketch, "E231", {"start": v(-3.5, -107.1) * mm, "end": v(-2.97, -107.06) * mm});
            skLineSegment(sketch, "E232", {"start": v(-2.97, -107.06) * mm, "end": v(-2.63, -106.96) * mm});
            skLineSegment(sketch, "E233", {"start": v(-2.63, -106.96) * mm, "end": v(-2.09, -106.88) * mm});
            skLineSegment(sketch, "E234", {"start": v(-2.09, -106.88) * mm, "end": v(-1.5, -106.84) * mm});
            skLineSegment(sketch, "E235", {"start": v(-1.5, -106.84) * mm, "end": v(-1.02, -106.84) * mm});
            skLineSegment(sketch, "E236", {"start": v(-1.02, -106.84) * mm, "end": v(-0.8, -106.8) * mm});
            skLineSegment(sketch, "E237", {"start": v(-0.8, -106.8) * mm, "end": v(-0.61, -106.66) * mm});
            skLineSegment(sketch, "E238", {"start": v(-0.61, -106.66) * mm, "end": v(-0.12, -106.63) * mm});
            skLineSegment(sketch, "E239", {"start": v(-0.12, -106.63) * mm, "end": v(0.54, -106.63) * mm});
            skLineSegment(sketch, "E240", {"start": v(0.54, -106.63) * mm, "end": v(0.98, -106.6) * mm});
            skLineSegment(sketch, "E241", {"start": v(0.98, -106.6) * mm, "end": v(1.23, -106.52) * mm});
            skLineSegment(sketch, "E242", {"start": v(1.23, -106.52) * mm, "end": v(1.48, -106.41) * mm});
            skLineSegment(sketch, "E243", {"start": v(1.48, -106.41) * mm, "end": v(1.9, -106.38) * mm});
            skLineSegment(sketch, "E244", {"start": v(1.9, -106.38) * mm, "end": v(2.3, -106.38) * mm});
            skLineSegment(sketch, "E245", {"start": v(2.3, -106.38) * mm, "end": v(2.81, -106.38) * mm});
            skLineSegment(sketch, "E246", {"start": v(2.81, -106.38) * mm, "end": v(3.96, -106.38) * mm});
            skLineSegment(sketch, "E247", {"start": v(3.96, -106.38) * mm, "end": v(4.99, -106.38) * mm});
            skLineSegment(sketch, "E248", {"start": v(4.99, -106.38) * mm, "end": v(7.97, -106.38) * mm});
            skLineSegment(sketch, "E249", {"start": v(7.97, -106.38) * mm, "end": v(12.2, -106.54) * mm});
            skLineSegment(sketch, "E250", {"start": v(12.2, -106.54) * mm, "end": v(14.88, -106.74) * mm});
            skLineSegment(sketch, "E251", {"start": v(14.88, -106.74) * mm, "end": v(18.17, -107.1) * mm});
            skLineSegment(sketch, "E252", {"start": v(18.17, -107.1) * mm, "end": v(21.16, -107.37) * mm});
            skLineSegment(sketch, "E253", {"start": v(21.16, -107.37) * mm, "end": v(24.7, -107.73) * mm});
            skLineSegment(sketch, "E254", {"start": v(24.7, -107.73) * mm, "end": v(27.23, -107.94) * mm});
            skLineSegment(sketch, "E255", {"start": v(27.23, -107.94) * mm, "end": v(28.88, -108.04) * mm});
            skLineSegment(sketch, "E256", {"start": v(28.88, -108.04) * mm, "end": v(29.54, -108.04) * mm});
            skLineSegment(sketch, "E257", {"start": v(29.54, -108.04) * mm, "end": v(30.16, -107.76) * mm});
            skLineSegment(sketch, "E258", {"start": v(30.16, -107.76) * mm, "end": v(30.52, -107.41) * mm});
            skLineSegment(sketch, "E259", {"start": v(30.52, -107.41) * mm, "end": v(30.96, -106.59) * mm});
            skLineSegment(sketch, "E260", {"start": v(30.96, -106.59) * mm, "end": v(31.75, -104.76) * mm});
            skLineSegment(sketch, "E261", {"start": v(31.75, -104.76) * mm, "end": v(32.44, -102.72) * mm});
            skLineSegment(sketch, "E262", {"start": v(32.44, -102.72) * mm, "end": v(32.88, -100.63) * mm});
            skLineSegment(sketch, "E263", {"start": v(32.88, -100.63) * mm, "end": v(33.43, -97.42) * mm});
            skLineSegment(sketch, "E264", {"start": v(33.43, -97.42) * mm, "end": v(34.75, -88.88) * mm});
            skLineSegment(sketch, "E265", {"start": v(34.75, -88.88) * mm, "end": v(35.1, -84.1) * mm});
            skLineSegment(sketch, "E266", {"start": v(35.1, -84.1) * mm, "end": v(35.1, -81.16) * mm});
            skLineSegment(sketch, "E267", {"start": v(35.1, -81.16) * mm, "end": v(35.1, -77.15) * mm});
            skLineSegment(sketch, "E268", {"start": v(35.1, -77.15) * mm, "end": v(34.91, -69.15) * mm});
            skLineSegment(sketch, "E269", {"start": v(34.91, -69.15) * mm, "end": v(34.89, -68.8) * mm});
            skLineSegment(sketch, "E270", {"start": v(34.89, -68.8) * mm, "end": v(34.89, -68.51) * mm});
            skLineSegment(sketch, "E271", {"start": v(34.89, -68.51) * mm, "end": v(34.91, -68.22) * mm});
            skLineSegment(sketch, "E272", {"start": v(34.91, -68.22) * mm, "end": v(35.12, -67.74) * mm});
            skLineSegment(sketch, "E273", {"start": v(35.12, -67.74) * mm, "end": v(35.55, -67.25) * mm});
            skLineSegment(sketch, "E274", {"start": v(35.55, -67.25) * mm, "end": v(37.03, -65.35) * mm});
            skLineSegment(sketch, "E275", {"start": v(37.03, -65.35) * mm, "end": v(38.06, -64.28) * mm});
            skLineSegment(sketch, "E276", {"start": v(38.06, -64.28) * mm, "end": v(40.21, -61.87) * mm});
            skLineSegment(sketch, "E277", {"start": v(40.21, -61.87) * mm, "end": v(43.72, -57.48) * mm});
            skLineSegment(sketch, "E278", {"start": v(43.72, -57.48) * mm, "end": v(44.98, -55.5) * mm});
            skLineSegment(sketch, "E279", {"start": v(44.98, -55.5) * mm, "end": v(45.84, -53.81) * mm});
            skLineSegment(sketch, "E280", {"start": v(45.84, -53.81) * mm, "end": v(46.15, -52.9) * mm});
            skLineSegment(sketch, "E281", {"start": v(46.15, -52.9) * mm, "end": v(46.25, -52.15) * mm});
            skLineSegment(sketch, "E282", {"start": v(46.25, -52.15) * mm, "end": v(46.33, -51.36) * mm});
            skLineSegment(sketch, "E283", {"start": v(46.33, -51.36) * mm, "end": v(46.38, -50.91) * mm});
            skLineSegment(sketch, "E284", {"start": v(46.38, -50.91) * mm, "end": v(46.4, -50.48) * mm});
            skLineSegment(sketch, "E285", {"start": v(46.4, -50.48) * mm, "end": v(46.4, -50.35) * mm});
            skLineSegment(sketch, "E286", {"start": v(46.4, -50.35) * mm, "end": v(46.43, -50.17) * mm});
            skLineSegment(sketch, "E287", {"start": v(46.43, -50.17) * mm, "end": v(46.45, -49.97) * mm});
            skLineSegment(sketch, "E288", {"start": v(46.45, -49.97) * mm, "end": v(46.5, -49.5) * mm});
            skLineSegment(sketch, "E289", {"start": v(46.5, -49.5) * mm, "end": v(46.56, -49.13) * mm});
            skLineSegment(sketch, "E290", {"start": v(46.56, -49.13) * mm, "end": v(46.57, -49.04) * mm});
            skLineSegment(sketch, "E291", {"start": v(46.57, -49.04) * mm, "end": v(46.57, -47.96) * mm});
            skLineSegment(sketch, "E292", {"start": v(46.57, -47.96) * mm, "end": v(46.57, -47.51) * mm});
            skLineSegment(sketch, "E293", {"start": v(46.57, -47.51) * mm, "end": v(46.45, -46.98) * mm});
            skLineSegment(sketch, "E294", {"start": v(46.45, -46.98) * mm, "end": v(46.38, -46.2) * mm});
            skLineSegment(sketch, "E295", {"start": v(46.38, -46.2) * mm, "end": v(46.26, -44.86) * mm});
            skLineSegment(sketch, "E296", {"start": v(46.26, -44.86) * mm, "end": v(46.26, -43.6) * mm});
            skLineSegment(sketch, "E297", {"start": v(46.26, -43.6) * mm, "end": v(46.17, -42.69) * mm});
            skLineSegment(sketch, "E298", {"start": v(46.17, -42.69) * mm, "end": v(45.95, -40.24) * mm});
            skLineSegment(sketch, "E299", {"start": v(45.95, -40.24) * mm, "end": v(45.82, -38.85) * mm});
            skLineSegment(sketch, "E300", {"start": v(45.82, -38.85) * mm, "end": v(45.62, -37.48) * mm});
            skLineSegment(sketch, "E301", {"start": v(45.62, -37.48) * mm, "end": v(45.4, -36.03) * mm});
            skLineSegment(sketch, "E302", {"start": v(45.4, -36.03) * mm, "end": v(45.27, -35.26) * mm});
            skLineSegment(sketch, "E303", {"start": v(45.27, -35.26) * mm, "end": v(44.6, -32.63) * mm});
            skLineSegment(sketch, "E304", {"start": v(44.6, -32.63) * mm, "end": v(44.24, -31.44) * mm});
            skLineSegment(sketch, "E305", {"start": v(44.24, -31.44) * mm, "end": v(43.13, -28.6) * mm});
            skLineSegment(sketch, "E306", {"start": v(43.13, -28.6) * mm, "end": v(42.58, -27.29) * mm});
            skLineSegment(sketch, "E307", {"start": v(42.58, -27.29) * mm, "end": v(42.07, -26.4) * mm});
            skLineSegment(sketch, "E308", {"start": v(42.07, -26.4) * mm, "end": v(41.25, -25.41) * mm});
            skLineSegment(sketch, "E309", {"start": v(41.25, -25.41) * mm, "end": v(39.82, -24.03) * mm});
            skLineSegment(sketch, "E310", {"start": v(39.82, -24.03) * mm, "end": v(38.09, -22.7) * mm});
            skLineSegment(sketch, "E311", {"start": v(38.09, -22.7) * mm, "end": v(35.9, -21.33) * mm});
            skLineSegment(sketch, "E312", {"start": v(35.9, -21.33) * mm, "end": v(34.34, -20.42) * mm});
            skLineSegment(sketch, "E313", {"start": v(34.34, -20.42) * mm, "end": v(33.2, -19.91) * mm});
            skLineSegment(sketch, "E314", {"start": v(33.2, -19.91) * mm, "end": v(32.58, -19.6) * mm});
            skLineSegment(sketch, "E315", {"start": v(32.58, -19.6) * mm, "end": v(31.86, -19.12) * mm});
            skLineSegment(sketch, "E316", {"start": v(31.86, -19.12) * mm, "end": v(30.87, -18.33) * mm});
            skLineSegment(sketch, "E317", {"start": v(30.87, -18.33) * mm, "end": v(29.4, -17.05) * mm});
            skLineSegment(sketch, "E318", {"start": v(29.4, -17.05) * mm, "end": v(28.36, -16.1) * mm});
            skLineSegment(sketch, "E319", {"start": v(28.36, -16.1) * mm, "end": v(27.54, -15.42) * mm});
            skLineSegment(sketch, "E320", {"start": v(27.54, -15.42) * mm, "end": v(25.7, -14.41) * mm});
            skLineSegment(sketch, "E321", {"start": v(25.7, -14.41) * mm, "end": v(23.9, -13.63) * mm});
            skLineSegment(sketch, "E322", {"start": v(23.9, -13.63) * mm, "end": v(20.9, -12.52) * mm});
            skLineSegment(sketch, "E323", {"start": v(20.9, -12.52) * mm, "end": v(17.87, -11.47) * mm});
            skLineSegment(sketch, "E324", {"start": v(17.87, -11.47) * mm, "end": v(15.3, -10.65) * mm});
            skLineSegment(sketch, "E325", {"start": v(15.3, -10.65) * mm, "end": v(13.72, -10.28) * mm});
            skLineSegment(sketch, "E326", {"start": v(13.72, -10.28) * mm, "end": v(12.86, -10.07) * mm});
            skLineSegment(sketch, "E327", {"start": v(12.86, -10.07) * mm, "end": v(12.41, -9.9) * mm});
            skLineSegment(sketch, "E328", {"start": v(12.41, -9.9) * mm, "end": v(12, -9.73) * mm});
            skLineSegment(sketch, "E329", {"start": v(12, -9.73) * mm, "end": v(11.7, -9.5) * mm});
            skLineSegment(sketch, "E330", {"start": v(11.7, -9.5) * mm, "end": v(11.6, -9.3) * mm});
            skLineSegment(sketch, "E331", {"start": v(11.6, -9.3) * mm, "end": v(11.4, -8.97) * mm});
            skLineSegment(sketch, "E332", {"start": v(11.4, -8.97) * mm, "end": v(11.27, -8.46) * mm});
            skLineSegment(sketch, "E333", {"start": v(11.27, -8.46) * mm, "end": v(11.14, -7.56) * mm});
            skLineSegment(sketch, "E334", {"start": v(11.14, -7.56) * mm, "end": v(10.93, -6.2) * mm});
            skLineSegment(sketch, "E335", {"start": v(10.93, -6.2) * mm, "end": v(10.93, -4.2) * mm});
            skLineSegment(sketch, "E336", {"start": v(10.93, -4.2) * mm, "end": v(10.93, -2.74) * mm});
            skLineSegment(sketch, "E337", {"start": v(10.93, -2.74) * mm, "end": v(10.75, 3.06) * mm});
            skLineSegment(sketch, "E338", {"start": v(10.75, 3.06) * mm, "end": v(10.61, 5.96) * mm});
            skLineSegment(sketch, "E339", {"start": v(10.61, 5.96) * mm, "end": v(10.42, 8.1) * mm});
            skLineSegment(sketch, "E340", {"start": v(10.42, 8.1) * mm, "end": v(10, 12.64) * mm});
            skLineSegment(sketch, "E341", {"start": v(10, 12.64) * mm, "end": v(9.44, 16.33) * mm});
            skLineSegment(sketch, "E342", {"start": v(9.44, 16.33) * mm, "end": v(9.05, 18.88) * mm});
            skLineSegment(sketch, "E343", {"start": v(9.05, 18.88) * mm, "end": v(8.76, 20.76) * mm});
            skLineSegment(sketch, "E344", {"start": v(8.76, 20.76) * mm, "end": v(8.5, 22.43) * mm});
            skLineSegment(sketch, "E345", {"start": v(8.5, 22.43) * mm, "end": v(8.35, 24.14) * mm});
            skLineSegment(sketch, "E346", {"start": v(8.35, 24.14) * mm, "end": v(8.24, 25.34) * mm});
            skLineSegment(sketch, "E347", {"start": v(8.24, 25.34) * mm, "end": v(8.12, 27.83) * mm});
            skLineSegment(sketch, "E348", {"start": v(8.12, 27.83) * mm, "end": v(7.88, 30.5) * mm});
            skLineSegment(sketch, "E349", {"start": v(7.88, 30.5) * mm, "end": v(7.71, 32.3) * mm});
            skLineSegment(sketch, "E350", {"start": v(7.71, 32.3) * mm, "end": v(7.63, 33.23) * mm});
            skLineSegment(sketch, "E351", {"start": v(7.63, 33.23) * mm, "end": v(7.28, 35.52) * mm});
            skLineSegment(sketch, "E352", {"start": v(7.28, 35.52) * mm, "end": v(7.07, 36.9) * mm});
            skLineSegment(sketch, "E353", {"start": v(7.07, 36.9) * mm, "end": v(6.6, 38.03) * mm});
            skLineSegment(sketch, "E354", {"start": v(6.6, 38.03) * mm, "end": v(5.92, 39.48) * mm});
            skLineSegment(sketch, "E355", {"start": v(5.92, 39.48) * mm, "end": v(5.59, 40.5) * mm});
            skLineSegment(sketch, "E356", {"start": v(5.59, 40.5) * mm, "end": v(5.37, 41.04) * mm});
            skLineSegment(sketch, "E357", {"start": v(5.37, 41.04) * mm, "end": v(5.2, 42.09) * mm});
            skLineSegment(sketch, "E358", {"start": v(5.2, 42.09) * mm, "end": v(4.95, 43.8) * mm});
            skLineSegment(sketch, "E359", {"start": v(4.95, 43.8) * mm, "end": v(4.78, 44.92) * mm});
            skLineSegment(sketch, "E360", {"start": v(4.78, 44.92) * mm, "end": v(4.4, 47.42) * mm});
            skLineSegment(sketch, "E361", {"start": v(4.4, 47.42) * mm, "end": v(4.12, 50.36) * mm});
            skLineSegment(sketch, "E362", {"start": v(4.12, 50.36) * mm, "end": v(3.61, 55.93) * mm});
            skLineSegment(sketch, "E363", {"start": v(3.61, 55.93) * mm, "end": v(2.93, 61.3) * mm});
            skLineSegment(sketch, "E364", {"start": v(2.93, 61.3) * mm, "end": v(2.4, 64.78) * mm});
            skLineSegment(sketch, "E365", {"start": v(2.4, 64.78) * mm, "end": v(2.26, 67.77) * mm});
            skLineSegment(sketch, "E366", {"start": v(2.26, 67.77) * mm, "end": v(2.26, 72.28) * mm});
            skLineSegment(sketch, "E367", {"start": v(2.26, 72.28) * mm, "end": v(2.26, 75) * mm});
            skLineSegment(sketch, "E368", {"start": v(2.26, 75) * mm, "end": v(2.34, 75.76) * mm});
            skLineSegment(sketch, "E369", {"start": v(2.34, 75.76) * mm, "end": v(2.6, 77.21) * mm});
            skLineSegment(sketch, "E370", {"start": v(2.6, 77.21) * mm, "end": v(3.05, 79.18) * mm});
            skLineSegment(sketch, "E371", {"start": v(3.05, 79.18) * mm, "end": v(3.5, 80.98) * mm});
            skLineSegment(sketch, "E372", {"start": v(3.5, 80.98) * mm, "end": v(4.29, 84.22) * mm});
            skLineSegment(sketch, "E373", {"start": v(4.29, 84.22) * mm, "end": v(4.7, 85.84) * mm});
            skLineSegment(sketch, "E374", {"start": v(4.7, 85.84) * mm, "end": v(5.03, 88.1) * mm});
            skLineSegment(sketch, "E375", {"start": v(5.03, 88.1) * mm, "end": v(5.34, 90.23) * mm});
            skLineSegment(sketch, "E376", {"start": v(5.34, 90.23) * mm, "end": v(5.65, 91.74) * mm});
            skLineSegment(sketch, "E377", {"start": v(5.65, 91.74) * mm, "end": v(6.2, 93.2) * mm});
            skLineSegment(sketch, "E378", {"start": v(6.2, 93.2) * mm, "end": v(6.5, 94.15) * mm});
            skLineSegment(sketch, "E379", {"start": v(6.5, 94.15) * mm, "end": v(6.74, 95.81) * mm});
            skLineSegment(sketch, "E380", {"start": v(6.74, 95.81) * mm, "end": v(6.9, 96.93) * mm});
            skLineSegment(sketch, "E381", {"start": v(6.9, 96.93) * mm, "end": v(7.03, 98.24) * mm});
            skLineSegment(sketch, "E382", {"start": v(7.03, 98.24) * mm, "end": v(7.17, 99.58) * mm});
            skLineSegment(sketch, "E383", {"start": v(7.17, 99.58) * mm, "end": v(7.3, 100.94) * mm});
            skLineSegment(sketch, "E384", {"start": v(7.3, 100.94) * mm, "end": v(7.74, 102.3) * mm});
            skLineSegment(sketch, "E385", {"start": v(7.74, 102.3) * mm, "end": v(8.19, 103.71) * mm});
            skLineSegment(sketch, "E386", {"start": v(8.19, 103.71) * mm, "end": v(8.78, 105.58) * mm});
            skLineSegment(sketch, "E387", {"start": v(8.78, 105.58) * mm, "end": v(9.26, 107.08) * mm});
            skLineSegment(sketch, "E388", {"start": v(9.26, 107.08) * mm, "end": v(9.58, 108.1) * mm});
            skLineSegment(sketch, "E389", {"start": v(9.58, 108.1) * mm, "end": v(9.58, 108.62) * mm});
            skLineSegment(sketch, "E390", {"start": v(9.58, 108.62) * mm, "end": v(9.77, 109.22) * mm});
            skLineSegment(sketch, "E391", {"start": v(9.77, 109.22) * mm, "end": v(10.1, 109.57) * mm});
            skLineSegment(sketch, "E392", {"start": v(10.1, 109.57) * mm, "end": v(10.29, 109.77) * mm});
            skLineSegment(sketch, "E393", {"start": v(10.29, 109.77) * mm, "end": v(10.32, 110.1) * mm});
            skLineSegment(sketch, "E394", {"start": v(10.32, 110.1) * mm, "end": v(10.44, 110.34) * mm});
            skLineSegment(sketch, "E395", {"start": v(10.44, 110.34) * mm, "end": v(10.61, 110.53) * mm});
            skLineSegment(sketch, "E396", {"start": v(10.61, 110.53) * mm, "end": v(10.7, 111) * mm});
            skLineSegment(sketch, "E397", {"start": v(10.7, 111) * mm, "end": v(10.62, 111.57) * mm});
            skLineSegment(sketch, "E398", {"start": v(10.62, 111.57) * mm, "end": v(10.38, 111.76) * mm});
            skLineSegment(sketch, "E399", {"start": v(10.38, 111.76) * mm, "end": v(10.23, 111.87) * mm});
            skLineSegment(sketch, "E400", {"start": v(10.23, 111.87) * mm, "end": v(6.83, 111.87) * mm});
            skLineSegment(sketch, "E401", {"start": v(-21.9, -44.9) * mm, "end": v(-23.58, -45.45) * mm});
            skLineSegment(sketch, "E402", {"start": v(-23.58, -45.45) * mm, "end": v(-25.28, -46.2) * mm});
            skLineSegment(sketch, "E403", {"start": v(-25.28, -46.2) * mm, "end": v(-26.99, -47.32) * mm});
            skLineSegment(sketch, "E404", {"start": v(-26.99, -47.32) * mm, "end": v(-28.02, -48.15) * mm});
            skLineSegment(sketch, "E405", {"start": v(-28.02, -48.15) * mm, "end": v(-29.18, -49.07) * mm});
            skLineSegment(sketch, "E406", {"start": v(-29.18, -49.07) * mm, "end": v(-30.03, -49.93) * mm});
            skLineSegment(sketch, "E407", {"start": v(-30.03, -49.93) * mm, "end": v(-30.65, -50.61) * mm});
            skLineSegment(sketch, "E408", {"start": v(-30.65, -50.61) * mm, "end": v(-31.06, -51.2) * mm});
            skLineSegment(sketch, "E409", {"start": v(-31.06, -51.2) * mm, "end": v(-31.3, -51.75) * mm});
            skLineSegment(sketch, "E410", {"start": v(-31.3, -51.75) * mm, "end": v(-31.36, -52.21) * mm});
            skLineSegment(sketch, "E411", {"start": v(-31.36, -52.21) * mm, "end": v(-31.36, -52.78) * mm});
            skLineSegment(sketch, "E412", {"start": v(-31.36, -52.78) * mm, "end": v(-31.2, -53.17) * mm});
            skLineSegment(sketch, "E413", {"start": v(-31.2, -53.17) * mm, "end": v(-30.8, -53.8) * mm});
            skLineSegment(sketch, "E414", {"start": v(-30.8, -53.8) * mm, "end": v(-29.63, -55.22) * mm});
            skLineSegment(sketch, "E415", {"start": v(-29.63, -55.22) * mm, "end": v(-28.78, -56.06) * mm});
            skLineSegment(sketch, "E416", {"start": v(-28.78, -56.06) * mm, "end": v(-27.56, -57.27) * mm});
            skLineSegment(sketch, "E417", {"start": v(-27.56, -57.27) * mm, "end": v(-26.7, -58.12) * mm});
            skLineSegment(sketch, "E418", {"start": v(-26.7, -58.12) * mm, "end": v(-25.76, -59.05) * mm});
            skLineSegment(sketch, "E419", {"start": v(-25.76, -59.05) * mm, "end": v(-25.06, -59.95) * mm});
            skLineSegment(sketch, "E420", {"start": v(-25.06, -59.95) * mm, "end": v(-24.29, -61.13) * mm});
            skLineSegment(sketch, "E421", {"start": v(-24.29, -61.13) * mm, "end": v(-23.42, -62.45) * mm});
            skLineSegment(sketch, "E422", {"start": v(-23.42, -62.45) * mm, "end": v(-22.72, -63.83) * mm});
            skLineSegment(sketch, "E423", {"start": v(-22.72, -63.83) * mm, "end": v(-22, -65.43) * mm});
            skLineSegment(sketch, "E424", {"start": v(-22, -65.43) * mm, "end": v(-21.45, -66.88) * mm});
            skLineSegment(sketch, "E425", {"start": v(-21.45, -66.88) * mm, "end": v(-20.86, -68.79) * mm});
            skLineSegment(sketch, "E426", {"start": v(-20.86, -68.79) * mm, "end": v(-20.3, -70.8) * mm});
            skLineSegment(sketch, "E427", {"start": v(-20.3, -70.8) * mm, "end": v(-19.47, -73.56) * mm});
            skLineSegment(sketch, "E428", {"start": v(-19.47, -73.56) * mm, "end": v(-18.33, -77.48) * mm});
            skLineSegment(sketch, "E429", {"start": v(-18.33, -77.48) * mm, "end": v(-17.47, -80.22) * mm});
            skLineSegment(sketch, "E430", {"start": v(-17.47, -80.22) * mm, "end": v(-16.1, -83.86) * mm});
            skLineSegment(sketch, "E431", {"start": v(-16.1, -83.86) * mm, "end": v(-14.67, -87.7) * mm});
            skLineSegment(sketch, "E432", {"start": v(-14.67, -87.7) * mm, "end": v(-13.4, -91.25) * mm});
            skLineSegment(sketch, "E433", {"start": v(-13.4, -91.25) * mm, "end": v(-13.1, -92.09) * mm});
            skLineSegment(sketch, "E434", {"start": v(-13.1, -92.09) * mm, "end": v(-12.95, -92.47) * mm});
            skLineSegment(sketch, "E435", {"start": v(-12.95, -92.47) * mm, "end": v(-12.74, -92.69) * mm});
            skLineSegment(sketch, "E436", {"start": v(-12.74, -92.69) * mm, "end": v(-12.35, -92.95) * mm});
            skLineSegment(sketch, "E437", {"start": v(-12.35, -92.95) * mm, "end": v(-11.25, -93.25) * mm});
            skLineSegment(sketch, "E438", {"start": v(-11.25, -93.25) * mm, "end": v(-10.15, -93.39) * mm});
            skLineSegment(sketch, "E439", {"start": v(-10.15, -93.39) * mm, "end": v(-9.73, -93.5) * mm});
            skLineSegment(sketch, "E440", {"start": v(-9.73, -93.5) * mm, "end": v(-8.33, -94.04) * mm});
            skLineSegment(sketch, "E441", {"start": v(-8.33, -94.04) * mm, "end": v(-7.14, -94.59) * mm});
            skLineSegment(sketch, "E442", {"start": v(-7.14, -94.59) * mm, "end": v(-5.87, -95.27) * mm});
            skLineSegment(sketch, "E443", {"start": v(-5.87, -95.27) * mm, "end": v(-5.01, -95.73) * mm});
            skLineSegment(sketch, "E444", {"start": v(-5.01, -95.73) * mm, "end": v(-4.26, -95.98) * mm});
            skLineSegment(sketch, "E445", {"start": v(-4.26, -95.98) * mm, "end": v(-2.58, -96.36) * mm});
            skLineSegment(sketch, "E446", {"start": v(-2.58, -96.36) * mm, "end": v(-0.52, -96.7) * mm});
            skLineSegment(sketch, "E447", {"start": v(-0.52, -96.7) * mm, "end": v(0.78, -96.93) * mm});
            skLineSegment(sketch, "E448", {"start": v(0.78, -96.93) * mm, "end": v(2.73, -97.17) * mm});
            skLineSegment(sketch, "E449", {"start": v(2.73, -97.17) * mm, "end": v(5.11, -97.3) * mm});
            skLineSegment(sketch, "E450", {"start": v(5.11, -97.3) * mm, "end": v(10.25, -97.4) * mm});
            skLineSegment(sketch, "E451", {"start": v(10.25, -97.4) * mm, "end": v(15.88, -97.52) * mm});
            skLineSegment(sketch, "E452", {"start": v(15.88, -97.52) * mm, "end": v(18.58, -97.52) * mm});
            skLineSegment(sketch, "E453", {"start": v(18.58, -97.52) * mm, "end": v(19.5, -97.34) * mm});
            skLineSegment(sketch, "E454", {"start": v(19.5, -97.34) * mm, "end": v(19.76, -96.94) * mm});
            skLineSegment(sketch, "E455", {"start": v(19.76, -96.94) * mm, "end": v(19.86, -94.6) * mm});
            skLineSegment(sketch, "E456", {"start": v(19.86, -94.6) * mm, "end": v(19.86, -92.15) * mm});
            skLineSegment(sketch, "E457", {"start": v(19.86, -92.15) * mm, "end": v(19.86, -89.55) * mm});
            skLineSegment(sketch, "E458", {"start": v(19.86, -89.55) * mm, "end": v(19.86, -87.06) * mm});
            skLineSegment(sketch, "E459", {"start": v(19.86, -87.06) * mm, "end": v(19.76, -84.03) * mm});
            skLineSegment(sketch, "E460", {"start": v(19.76, -84.03) * mm, "end": v(19.66, -81.86) * mm});
            skLineSegment(sketch, "E461", {"start": v(19.66, -81.86) * mm, "end": v(19.66, -81.67) * mm});
            skLineSegment(sketch, "E462", {"start": v(19.66, -81.67) * mm, "end": v(19.63, -81.57) * mm});
            skLineSegment(sketch, "E463", {"start": v(19.63, -81.57) * mm, "end": v(19.53, -81.5) * mm});
            skLineSegment(sketch, "E464", {"start": v(19.53, -81.5) * mm, "end": v(19.4, -81.48) * mm});
            skLineSegment(sketch, "E465", {"start": v(19.4, -81.48) * mm, "end": v(19.26, -81.54) * mm});
            skLineSegment(sketch, "E466", {"start": v(19.26, -81.54) * mm, "end": v(19.07, -81.6) * mm});
            skLineSegment(sketch, "E467", {"start": v(19.07, -81.6) * mm, "end": v(18.64, -81.98) * mm});
            skLineSegment(sketch, "E468", {"start": v(18.64, -81.98) * mm, "end": v(18.27, -82.4) * mm});
            skLineSegment(sketch, "E469", {"start": v(18.27, -82.4) * mm, "end": v(17.25, -83.72) * mm});
            skLineSegment(sketch, "E470", {"start": v(17.25, -83.72) * mm, "end": v(16.85, -84.34) * mm});
            skLineSegment(sketch, "E471", {"start": v(16.85, -84.34) * mm, "end": v(16.26, -85.43) * mm});
            skLineSegment(sketch, "E472", {"start": v(16.26, -85.43) * mm, "end": v(15.98, -86.13) * mm});
            skLineSegment(sketch, "E473", {"start": v(15.98, -86.13) * mm, "end": v(15.62, -87.48) * mm});
            skLineSegment(sketch, "E474", {"start": v(15.62, -87.48) * mm, "end": v(15.49, -87.98) * mm});
            skLineSegment(sketch, "E475", {"start": v(15.49, -87.98) * mm, "end": v(15.3, -88.37) * mm});
            skLineSegment(sketch, "E476", {"start": v(15.3, -88.37) * mm, "end": v(14.98, -88.64) * mm});
            skLineSegment(sketch, "E477", {"start": v(14.98, -88.64) * mm, "end": v(14.64, -88.8) * mm});
            skLineSegment(sketch, "E478", {"start": v(14.64, -88.8) * mm, "end": v(14.25, -88.91) * mm});
            skLineSegment(sketch, "E479", {"start": v(14.25, -88.91) * mm, "end": v(13.9, -88.91) * mm});
            skLineSegment(sketch, "E480", {"start": v(13.9, -88.91) * mm, "end": v(13.5, -88.8) * mm});
            skLineSegment(sketch, "E481", {"start": v(13.5, -88.8) * mm, "end": v(13.08, -88.61) * mm});
            skLineSegment(sketch, "E482", {"start": v(13.08, -88.61) * mm, "end": v(12.93, -88.46) * mm});
            skLineSegment(sketch, "E483", {"start": v(12.93, -88.46) * mm, "end": v(12.77, -88.27) * mm});
            skLineSegment(sketch, "E484", {"start": v(12.77, -88.27) * mm, "end": v(12.52, -88.2) * mm});
            skLineSegment(sketch, "E485", {"start": v(12.52, -88.2) * mm, "end": v(12.24, -88.2) * mm});
            skLineSegment(sketch, "E486", {"start": v(12.24, -88.2) * mm, "end": v(11.91, -88.2) * mm});
            skLineSegment(sketch, "E487", {"start": v(11.91, -88.2) * mm, "end": v(11.72, -88.27) * mm});
            skLineSegment(sketch, "E488", {"start": v(11.72, -88.27) * mm, "end": v(11.37, -88.43) * mm});
            skLineSegment(sketch, "E489", {"start": v(11.37, -88.43) * mm, "end": v(11.1, -88.63) * mm});
            skLineSegment(sketch, "E490", {"start": v(11.1, -88.63) * mm, "end": v(10.86, -88.68) * mm});
            skLineSegment(sketch, "E491", {"start": v(10.86, -88.68) * mm, "end": v(10.55, -88.7) * mm});
            skLineSegment(sketch, "E492", {"start": v(10.55, -88.7) * mm, "end": v(10.15, -88.46) * mm});
            skLineSegment(sketch, "E493", {"start": v(10.15, -88.46) * mm, "end": v(9.92, -88.21) * mm});
            skLineSegment(sketch, "E494", {"start": v(9.92, -88.21) * mm, "end": v(9.88, -88.06) * mm});
            skLineSegment(sketch, "E495", {"start": v(9.88, -88.06) * mm, "end": v(9.88, -87.95) * mm});
            skLineSegment(sketch, "E496", {"start": v(9.88, -87.95) * mm, "end": v(9.83, -87.82) * mm});
            skLineSegment(sketch, "E497", {"start": v(9.83, -87.82) * mm, "end": v(9.68, -87.75) * mm});
            skLineSegment(sketch, "E498", {"start": v(9.68, -87.75) * mm, "end": v(9.5, -87.75) * mm});
            skLineSegment(sketch, "E499", {"start": v(9.5, -87.75) * mm, "end": v(9.06, -87.98) * mm});
            skLineSegment(sketch, "E500", {"start": v(9.06, -87.98) * mm, "end": v(8.58, -88.2) * mm});
            skLineSegment(sketch, "E501", {"start": v(8.58, -88.2) * mm, "end": v(8.23, -88.26) * mm});
            skLineSegment(sketch, "E502", {"start": v(8.23, -88.26) * mm, "end": v(8.05, -88.22) * mm});
            skLineSegment(sketch, "E503", {"start": v(8.05, -88.22) * mm, "end": v(7.62, -87.8) * mm});
            skLineSegment(sketch, "E504", {"start": v(7.62, -87.8) * mm, "end": v(7.1, -87.28) * mm});
            skLineSegment(sketch, "E505", {"start": v(7.1, -87.28) * mm, "end": v(6.86, -87.05) * mm});
            skLineSegment(sketch, "E506", {"start": v(6.86, -87.05) * mm, "end": v(6.65, -86.88) * mm});
            skLineSegment(sketch, "E507", {"start": v(6.65, -86.88) * mm, "end": v(6.38, -86.8) * mm});
            skLineSegment(sketch, "E508", {"start": v(6.38, -86.8) * mm, "end": v(5.94, -86.8) * mm});
            skLineSegment(sketch, "E509", {"start": v(5.94, -86.8) * mm, "end": v(5.49, -86.8) * mm});
            skLineSegment(sketch, "E510", {"start": v(5.49, -86.8) * mm, "end": v(5.32, -86.96) * mm});
            skLineSegment(sketch, "E511", {"start": v(5.32, -86.96) * mm, "end": v(4.95, -87.48) * mm});
            skLineSegment(sketch, "E512", {"start": v(4.95, -87.48) * mm, "end": v(4.68, -87.77) * mm});
            skLineSegment(sketch, "E513", {"start": v(4.68, -87.77) * mm, "end": v(4.4, -87.95) * mm});
            skLineSegment(sketch, "E514", {"start": v(4.4, -87.95) * mm, "end": v(3.97, -88.06) * mm});
            skLineSegment(sketch, "E515", {"start": v(3.97, -88.06) * mm, "end": v(3.62, -88.06) * mm});
            skLineSegment(sketch, "E516", {"start": v(3.62, -88.06) * mm, "end": v(3.32, -87.9) * mm});
            skLineSegment(sketch, "E517", {"start": v(3.32, -87.9) * mm, "end": v(2.71, -86.96) * mm});
            skLineSegment(sketch, "E518", {"start": v(2.71, -86.96) * mm, "end": v(1.87, -85.25) * mm});
            skLineSegment(sketch, "E519", {"start": v(1.87, -85.25) * mm, "end": v(1.4, -84.3) * mm});
            skLineSegment(sketch, "E520", {"start": v(1.4, -84.3) * mm, "end": v(0.88, -83.59) * mm});
            skLineSegment(sketch, "E521", {"start": v(0.88, -83.59) * mm, "end": v(-0.22, -82.65) * mm});
            skLineSegment(sketch, "E522", {"start": v(-0.22, -82.65) * mm, "end": v(-1.7, -81.65) * mm});
            skLineSegment(sketch, "E523", {"start": v(-1.7, -81.65) * mm, "end": v(-2.82, -81) * mm});
            skLineSegment(sketch, "E524", {"start": v(-2.82, -81) * mm, "end": v(-3.62, -80.53) * mm});
            skLineSegment(sketch, "E525", {"start": v(-3.62, -80.53) * mm, "end": v(-4.47, -79.92) * mm});
            skLineSegment(sketch, "E526", {"start": v(-4.47, -79.92) * mm, "end": v(-5.27, -79.13) * mm});
            skLineSegment(sketch, "E527", {"start": v(-5.27, -79.13) * mm, "end": v(-5.53, -78.9) * mm});
            skLineSegment(sketch, "E528", {"start": v(-5.53, -78.9) * mm, "end": v(-5.64, -78.78) * mm});
            skLineSegment(sketch, "E529", {"start": v(-5.64, -78.78) * mm, "end": v(-5.76, -78.74) * mm});
            skLineSegment(sketch, "E530", {"start": v(-5.76, -78.74) * mm, "end": v(-5.81, -78.8) * mm});
            skLineSegment(sketch, "E531", {"start": v(-5.81, -78.8) * mm, "end": v(-5.88, -78.93) * mm});
            skLineSegment(sketch, "E532", {"start": v(-5.88, -78.93) * mm, "end": v(-5.93, -80.6) * mm});
            skLineSegment(sketch, "E533", {"start": v(-5.93, -80.6) * mm, "end": v(-5.93, -81.18) * mm});
            skLineSegment(sketch, "E534", {"start": v(-5.93, -81.18) * mm, "end": v(-5.92, -81.65) * mm});
            skLineSegment(sketch, "E535", {"start": v(-5.92, -81.65) * mm, "end": v(-5.88, -81.95) * mm});
            skLineSegment(sketch, "E536", {"start": v(-5.88, -81.95) * mm, "end": v(-5.7, -82.32) * mm});
            skLineSegment(sketch, "E537", {"start": v(-5.7, -82.32) * mm, "end": v(-5.22, -82.92) * mm});
            skLineSegment(sketch, "E538", {"start": v(-5.22, -82.92) * mm, "end": v(-4.73, -83.41) * mm});
            skLineSegment(sketch, "E539", {"start": v(-4.73, -83.41) * mm, "end": v(-4.57, -83.56) * mm});
            skLineSegment(sketch, "E540", {"start": v(-4.57, -83.56) * mm, "end": v(-5.46, -83.59) * mm});
            skLineSegment(sketch, "E541", {"start": v(-5.46, -83.59) * mm, "end": v(-5.41, -83.92) * mm});
            skLineSegment(sketch, "E542", {"start": v(-5.41, -83.92) * mm, "end": v(-5.28, -84.38) * mm});
            skLineSegment(sketch, "E543", {"start": v(-5.28, -84.38) * mm, "end": v(-5.02, -84.77) * mm});
            skLineSegment(sketch, "E544", {"start": v(-5.02, -84.77) * mm, "end": v(-4.81, -84.94) * mm});
            skLineSegment(sketch, "E545", {"start": v(-4.81, -84.94) * mm, "end": v(-4.81, -85.1) * mm});
            skLineSegment(sketch, "E546", {"start": v(-4.81, -85.1) * mm, "end": v(-5.05, -85.15) * mm});
            skLineSegment(sketch, "E547", {"start": v(-5.05, -85.15) * mm, "end": v(-5.15, -85.32) * mm});
            skLineSegment(sketch, "E548", {"start": v(-5.15, -85.32) * mm, "end": v(-5.15, -85.46) * mm});
            skLineSegment(sketch, "E549", {"start": v(-5.15, -85.46) * mm, "end": v(-5.9, -85.46) * mm});
            skLineSegment(sketch, "E550", {"start": v(-5.9, -85.46) * mm, "end": v(-7.07, -84.5) * mm});
            skLineSegment(sketch, "E551", {"start": v(-7.07, -84.5) * mm, "end": v(-7.16, -84.03) * mm});
            skLineSegment(sketch, "E552", {"start": v(-7.16, -84.03) * mm, "end": v(-7.56, -83.42) * mm});
            skLineSegment(sketch, "E553", {"start": v(-7.56, -83.42) * mm, "end": v(-7.82, -82.89) * mm});
            skLineSegment(sketch, "E554", {"start": v(-7.82, -82.89) * mm, "end": v(-8.23, -82.63) * mm});
            skLineSegment(sketch, "E555", {"start": v(-8.23, -82.63) * mm, "end": v(-8.28, -83.06) * mm});
            skLineSegment(sketch, "E556", {"start": v(-8.28, -83.06) * mm, "end": v(-8.08, -83.59) * mm});
            skLineSegment(sketch, "E557", {"start": v(-8.08, -83.59) * mm, "end": v(-7.47, -84.83) * mm});
            skLineSegment(sketch, "E558", {"start": v(-7.47, -84.83) * mm, "end": v(-6.78, -86.07) * mm});
            skLineSegment(sketch, "E559", {"start": v(-6.78, -86.07) * mm, "end": v(-6.53, -86.55) * mm});
            skLineSegment(sketch, "E560", {"start": v(-6.53, -86.55) * mm, "end": v(-6.53, -86.62) * mm});
            skLineSegment(sketch, "E561", {"start": v(-6.53, -86.62) * mm, "end": v(-6.97, -86.64) * mm});
            skLineSegment(sketch, "E562", {"start": v(-6.97, -86.64) * mm, "end": v(-7.57, -86.5) * mm});
            skLineSegment(sketch, "E563", {"start": v(-7.57, -86.5) * mm, "end": v(-8.7, -85.67) * mm});
            skLineSegment(sketch, "E564", {"start": v(-8.7, -85.67) * mm, "end": v(-9.53, -85.1) * mm});
            skLineSegment(sketch, "E565", {"start": v(-9.53, -85.1) * mm, "end": v(-10.44, -83.71) * mm});
            skLineSegment(sketch, "E566", {"start": v(-10.44, -83.71) * mm, "end": v(-11.02, -82.54) * mm});
            skLineSegment(sketch, "E567", {"start": v(-11.02, -82.54) * mm, "end": v(-11.1, -81.65) * mm});
            skLineSegment(sketch, "E568", {"start": v(-11.1, -81.65) * mm, "end": v(-11.1, -80.51) * mm});
            skLineSegment(sketch, "E569", {"start": v(-11.1, -80.51) * mm, "end": v(-11.1, -79.66) * mm});
            skLineSegment(sketch, "E570", {"start": v(-11.1, -79.66) * mm, "end": v(-11.1, -79.16) * mm});
            skLineSegment(sketch, "E571", {"start": v(-11.1, -79.16) * mm, "end": v(-11.52, -79.66) * mm});
            skLineSegment(sketch, "E572", {"start": v(-11.52, -79.66) * mm, "end": v(-11.74, -80.14) * mm});
            skLineSegment(sketch, "E573", {"start": v(-11.74, -80.14) * mm, "end": v(-11.95, -80.97) * mm});
            skLineSegment(sketch, "E574", {"start": v(-11.95, -80.97) * mm, "end": v(-12.04, -81.71) * mm});
            skLineSegment(sketch, "E575", {"start": v(-12.04, -81.71) * mm, "end": v(-11.98, -82.57) * mm});
            skLineSegment(sketch, "E576", {"start": v(-11.98, -82.57) * mm, "end": v(-11.7, -83.33) * mm});
            skLineSegment(sketch, "E577", {"start": v(-11.7, -83.33) * mm, "end": v(-11.23, -84.13) * mm});
            skLineSegment(sketch, "E578", {"start": v(-11.23, -84.13) * mm, "end": v(-12.08, -83.3) * mm});
            skLineSegment(sketch, "E579", {"start": v(-12.08, -83.3) * mm, "end": v(-12.26, -82.64) * mm});
            skLineSegment(sketch, "E580", {"start": v(-12.26, -82.64) * mm, "end": v(-12.42, -81.68) * mm});
            skLineSegment(sketch, "E581", {"start": v(-12.42, -81.68) * mm, "end": v(-12.5, -80.47) * mm});
            skLineSegment(sketch, "E582", {"start": v(-12.5, -80.47) * mm, "end": v(-12.12, -79.03) * mm});
            skLineSegment(sketch, "E583", {"start": v(-12.12, -79.03) * mm, "end": v(-11.44, -77.45) * mm});
            skLineSegment(sketch, "E584", {"start": v(-11.44, -77.45) * mm, "end": v(-9.63, -73.83) * mm});
            skLineSegment(sketch, "E585", {"start": v(-9.63, -73.83) * mm, "end": v(-9.2, -73) * mm});
            skLineSegment(sketch, "E586", {"start": v(-9.2, -73) * mm, "end": v(-9.03, -72.6) * mm});
            skLineSegment(sketch, "E587", {"start": v(-9.03, -72.6) * mm, "end": v(-9.15, -72.29) * mm});
            skLineSegment(sketch, "E588", {"start": v(-9.15, -72.29) * mm, "end": v(-10.01, -71.19) * mm});
            skLineSegment(sketch, "E589", {"start": v(-10.01, -71.19) * mm, "end": v(-10.34, -70.73) * mm});
            skLineSegment(sketch, "E590", {"start": v(-10.34, -70.73) * mm, "end": v(-10.48, -70.04) * mm});
            skLineSegment(sketch, "E591", {"start": v(-10.48, -70.04) * mm, "end": v(-10.48, -69.32) * mm});
            skLineSegment(sketch, "E592", {"start": v(-10.48, -69.32) * mm, "end": v(-10.3, -67.69) * mm});
            skLineSegment(sketch, "E593", {"start": v(-10.3, -67.69) * mm, "end": v(-10.04, -66.61) * mm});
            skLineSegment(sketch, "E594", {"start": v(-10.04, -66.61) * mm, "end": v(-8.54, -63.02) * mm});
            skLineSegment(sketch, "E595", {"start": v(-8.54, -63.02) * mm, "end": v(-7.1, -61.18) * mm});
            skLineSegment(sketch, "E596", {"start": v(-7.1, -61.18) * mm, "end": v(-5.3, -59.79) * mm});
            skLineSegment(sketch, "E597", {"start": v(-5.3, -59.79) * mm, "end": v(-2.78, -58.32) * mm});
            skLineSegment(sketch, "E598", {"start": v(-2.78, -58.32) * mm, "end": v(-1.19, -57.46) * mm});
            skLineSegment(sketch, "E599", {"start": v(-1.19, -57.46) * mm, "end": v(-0.32, -57.16) * mm});
            skLineSegment(sketch, "E600", {"start": v(-0.32, -57.16) * mm, "end": v(0, -57) * mm});
            skLineSegment(sketch, "E601", {"start": v(0, -57) * mm, "end": v(0.14, -56.93) * mm});
            skLineSegment(sketch, "E602", {"start": v(0.14, -56.93) * mm, "end": v(0.31, -56.76) * mm});
            skLineSegment(sketch, "E603", {"start": v(0.31, -56.76) * mm, "end": v(0.26, -56.33) * mm});
            skLineSegment(sketch, "E604", {"start": v(0.26, -56.33) * mm, "end": v(0.1, -56.17) * mm});
            skLineSegment(sketch, "E605", {"start": v(0.1, -56.17) * mm, "end": v(-0.82, -56.15) * mm});
            skLineSegment(sketch, "E606", {"start": v(-0.82, -56.15) * mm, "end": v(-2.31, -56.29) * mm});
            skLineSegment(sketch, "E607", {"start": v(-2.31, -56.29) * mm, "end": v(-3.07, -56.17) * mm});
            skLineSegment(sketch, "E608", {"start": v(-3.07, -56.17) * mm, "end": v(-3.86, -56.16) * mm});
            skLineSegment(sketch, "E609", {"start": v(-3.86, -56.16) * mm, "end": v(-4.5, -56.06) * mm});
            skLineSegment(sketch, "E610", {"start": v(-4.5, -56.06) * mm, "end": v(-3.49, -55.76) * mm});
            skLineSegment(sketch, "E611", {"start": v(-3.49, -55.76) * mm, "end": v(-2.8, -55.51) * mm});
            skLineSegment(sketch, "E612", {"start": v(-2.8, -55.51) * mm, "end": v(-2.65, -55.37) * mm});
            skLineSegment(sketch, "E613", {"start": v(-2.65, -55.37) * mm, "end": v(-2.98, -54.7) * mm});
            skLineSegment(sketch, "E614", {"start": v(-2.98, -54.7) * mm, "end": v(-3.24, -53.86) * mm});
            skLineSegment(sketch, "E615", {"start": v(-3.24, -53.86) * mm, "end": v(-3.6, -52.88) * mm});
            skLineSegment(sketch, "E616", {"start": v(-3.6, -52.88) * mm, "end": v(-3.6, -52.67) * mm});
            skLineSegment(sketch, "E617", {"start": v(-3.6, -52.67) * mm, "end": v(-3.63, -52.45) * mm});
            skLineSegment(sketch, "E618", {"start": v(-3.63, -52.45) * mm, "end": v(-3.84, -52.34) * mm});
            skLineSegment(sketch, "E619", {"start": v(-3.84, -52.34) * mm, "end": v(-4.09, -52.43) * mm});
            skLineSegment(sketch, "E620", {"start": v(-4.09, -52.43) * mm, "end": v(-4.56, -52.74) * mm});
            skLineSegment(sketch, "E621", {"start": v(-4.56, -52.74) * mm, "end": v(-5.31, -53.5) * mm});
            skLineSegment(sketch, "E622", {"start": v(-5.31, -53.5) * mm, "end": v(-5.8, -54.35) * mm});
            skLineSegment(sketch, "E623", {"start": v(-5.8, -54.35) * mm, "end": v(-6.21, -54.92) * mm});
            skLineSegment(sketch, "E624", {"start": v(-6.21, -54.92) * mm, "end": v(-6.6, -55.44) * mm});
            skLineSegment(sketch, "E625", {"start": v(-6.6, -55.44) * mm, "end": v(-6.9, -55.45) * mm});
            skLineSegment(sketch, "E626", {"start": v(-6.9, -55.45) * mm, "end": v(-6.9, -55.19) * mm});
            skLineSegment(sketch, "E627", {"start": v(-6.9, -55.19) * mm, "end": v(-5.97, -53.62) * mm});
            skLineSegment(sketch, "E628", {"start": v(-5.97, -53.62) * mm, "end": v(-5.36, -53.2) * mm});
            skLineSegment(sketch, "E629", {"start": v(-5.36, -53.2) * mm, "end": v(-5.05, -52.66) * mm});
            skLineSegment(sketch, "E630", {"start": v(-5.05, -52.66) * mm, "end": v(-4.76, -51.96) * mm});
            skLineSegment(sketch, "E631", {"start": v(-4.76, -51.96) * mm, "end": v(-4.56, -51.8) * mm});
            skLineSegment(sketch, "E632", {"start": v(-4.56, -51.8) * mm, "end": v(-4.54, -51.41) * mm});
            skLineSegment(sketch, "E633", {"start": v(-4.54, -51.41) * mm, "end": v(-4.76, -50.98) * mm});
            skLineSegment(sketch, "E634", {"start": v(-4.76, -50.98) * mm, "end": v(-5.12, -50.6) * mm});
            skLineSegment(sketch, "E635", {"start": v(-5.12, -50.6) * mm, "end": v(-5.51, -50.21) * mm});
            skLineSegment(sketch, "E636", {"start": v(-5.51, -50.21) * mm, "end": v(-5.67, -50.1) * mm});
            skLineSegment(sketch, "E637", {"start": v(-5.67, -50.1) * mm, "end": v(-5.98, -50.32) * mm});
            skLineSegment(sketch, "E638", {"start": v(-5.98, -50.32) * mm, "end": v(-6.13, -50.75) * mm});
            skLineSegment(sketch, "E639", {"start": v(-6.13, -50.75) * mm, "end": v(-6.3, -50.73) * mm});
            skLineSegment(sketch, "E640", {"start": v(-6.3, -50.73) * mm, "end": v(-6.34, -51.18) * mm});
            skLineSegment(sketch, "E641", {"start": v(-6.34, -51.18) * mm, "end": v(-6.53, -51.2) * mm});
            skLineSegment(sketch, "E642", {"start": v(-6.53, -51.2) * mm, "end": v(-6.53, -51.47) * mm});
            skLineSegment(sketch, "E643", {"start": v(-6.53, -51.47) * mm, "end": v(-6.73, -51.5) * mm});
            skLineSegment(sketch, "E644", {"start": v(-6.73, -51.5) * mm, "end": v(-6.78, -51.91) * mm});
            skLineSegment(sketch, "E645", {"start": v(-6.78, -51.91) * mm, "end": v(-7.02, -51.93) * mm});
            skLineSegment(sketch, "E646", {"start": v(-7.02, -51.93) * mm, "end": v(-7, -52.17) * mm});
            skLineSegment(sketch, "E647", {"start": v(-7, -52.17) * mm, "end": v(-7.72, -53.1) * mm});
            skLineSegment(sketch, "E648", {"start": v(-7.72, -53.1) * mm, "end": v(-7.26, -51.44) * mm});
            skLineSegment(sketch, "E649", {"start": v(-7.26, -51.44) * mm, "end": v(-6.42, -50.3) * mm});
            skLineSegment(sketch, "E650", {"start": v(-6.42, -50.3) * mm, "end": v(-6, -49.88) * mm});
            skLineSegment(sketch, "E651", {"start": v(-6, -49.88) * mm, "end": v(-5.8, -49.62) * mm});
            skLineSegment(sketch, "E652", {"start": v(-5.8, -49.62) * mm, "end": v(-6.06, -49.41) * mm});
            skLineSegment(sketch, "E653", {"start": v(-6.06, -49.41) * mm, "end": v(-6.57, -49.35) * mm});
            skLineSegment(sketch, "E654", {"start": v(-6.57, -49.35) * mm, "end": v(-7.46, -50.4) * mm});
            skLineSegment(sketch, "E655", {"start": v(-7.46, -50.4) * mm, "end": v(-8.57, -51.97) * mm});
            skLineSegment(sketch, "E656", {"start": v(-8.57, -51.97) * mm, "end": v(-9.1, -53.24) * mm});
            skLineSegment(sketch, "E657", {"start": v(-9.1, -53.24) * mm, "end": v(-9.61, -54.45) * mm});
            skLineSegment(sketch, "E658", {"start": v(-9.61, -54.45) * mm, "end": v(-10.1, -56.06) * mm});
            skLineSegment(sketch, "E659", {"start": v(-10.1, -56.06) * mm, "end": v(-9.86, -54.13) * mm});
            skLineSegment(sketch, "E660", {"start": v(-9.86, -54.13) * mm, "end": v(-9.44, -52.42) * mm});
            skLineSegment(sketch, "E661", {"start": v(-9.44, -52.42) * mm, "end": v(-8.09, -50.3) * mm});
            skLineSegment(sketch, "E662", {"start": v(-8.09, -50.3) * mm, "end": v(-6.46, -48.65) * mm});
            skLineSegment(sketch, "E663", {"start": v(-6.46, -48.65) * mm, "end": v(-5.7, -48.37) * mm});
            skLineSegment(sketch, "E664", {"start": v(-5.7, -48.37) * mm, "end": v(-4.48, -48.12) * mm});
            skLineSegment(sketch, "E665", {"start": v(-4.48, -48.12) * mm, "end": v(-3.66, -47.83) * mm});
            skLineSegment(sketch, "E666", {"start": v(-3.66, -47.83) * mm, "end": v(-3.25, -47.49) * mm});
            skLineSegment(sketch, "E667", {"start": v(-3.25, -47.49) * mm, "end": v(-3.2, -47.19) * mm});
            skLineSegment(sketch, "E668", {"start": v(-3.2, -47.19) * mm, "end": v(-3.74, -46.67) * mm});
            skLineSegment(sketch, "E669", {"start": v(-3.74, -46.67) * mm, "end": v(-4.24, -46.24) * mm});
            skLineSegment(sketch, "E670", {"start": v(-4.24, -46.24) * mm, "end": v(-2.9, -46.14) * mm});
            skLineSegment(sketch, "E671", {"start": v(-2.9, -46.14) * mm, "end": v(-1.7, -46.42) * mm});
            skLineSegment(sketch, "E672", {"start": v(-1.7, -46.42) * mm, "end": v(-0.56, -46.88) * mm});
            skLineSegment(sketch, "E673", {"start": v(-0.56, -46.88) * mm, "end": v(0.49, -47.32) * mm});
            skLineSegment(sketch, "E674", {"start": v(0.49, -47.32) * mm, "end": v(0.77, -47.36) * mm});
            skLineSegment(sketch, "E675", {"start": v(0.77, -47.36) * mm, "end": v(1.76, -47) * mm});
            skLineSegment(sketch, "E676", {"start": v(1.76, -47) * mm, "end": v(2.8, -46.48) * mm});
            skLineSegment(sketch, "E677", {"start": v(2.8, -46.48) * mm, "end": v(3.5, -46.43) * mm});
            skLineSegment(sketch, "E678", {"start": v(3.5, -46.43) * mm, "end": v(4.42, -46.52) * mm});
            skLineSegment(sketch, "E679", {"start": v(4.42, -46.52) * mm, "end": v(5.12, -46.82) * mm});
            skLineSegment(sketch, "E680", {"start": v(5.12, -46.82) * mm, "end": v(5.97, -47.42) * mm});
            skLineSegment(sketch, "E681", {"start": v(5.97, -47.42) * mm, "end": v(6.74, -48.19) * mm});
            skLineSegment(sketch, "E682", {"start": v(6.74, -48.19) * mm, "end": v(7.47, -49.3) * mm});
            skLineSegment(sketch, "E683", {"start": v(7.47, -49.3) * mm, "end": v(7.77, -50.11) * mm});
            skLineSegment(sketch, "E684", {"start": v(7.77, -50.11) * mm, "end": v(7.9, -50.93) * mm});
            skLineSegment(sketch, "E685", {"start": v(7.9, -50.93) * mm, "end": v(7.74, -52.4) * mm});
            skLineSegment(sketch, "E686", {"start": v(7.74, -52.4) * mm, "end": v(7.25, -53.52) * mm});
            skLineSegment(sketch, "E687", {"start": v(7.25, -53.52) * mm, "end": v(6.37, -54.22) * mm});
            skLineSegment(sketch, "E688", {"start": v(6.37, -54.22) * mm, "end": v(5.7, -54.46) * mm});
            skLineSegment(sketch, "E689", {"start": v(5.7, -54.46) * mm, "end": v(4.88, -54.7) * mm});
            skLineSegment(sketch, "E690", {"start": v(4.88, -54.7) * mm, "end": v(4.48, -54.9) * mm});
            skLineSegment(sketch, "E691", {"start": v(4.48, -54.9) * mm, "end": v(4.44, -55.5) * mm});
            skLineSegment(sketch, "E692", {"start": v(4.44, -55.5) * mm, "end": v(4.78, -55.9) * mm});
            skLineSegment(sketch, "E693", {"start": v(4.78, -55.9) * mm, "end": v(6.09, -55.9) * mm});
            skLineSegment(sketch, "E694", {"start": v(6.09, -55.9) * mm, "end": v(7.8, -55.37) * mm});
            skLineSegment(sketch, "E695", {"start": v(7.8, -55.37) * mm, "end": v(9.56, -54.13) * mm});
            skLineSegment(sketch, "E696", {"start": v(9.56, -54.13) * mm, "end": v(10.66, -53.75) * mm});
            skLineSegment(sketch, "E697", {"start": v(10.66, -53.75) * mm, "end": v(12.08, -53.65) * mm});
            skLineSegment(sketch, "E698", {"start": v(12.08, -53.65) * mm, "end": v(13.39, -53.66) * mm});
            skLineSegment(sketch, "E699", {"start": v(13.39, -53.66) * mm, "end": v(14.66, -53.96) * mm});
            skLineSegment(sketch, "E700", {"start": v(14.66, -53.96) * mm, "end": v(15.43, -54.28) * mm});
            skLineSegment(sketch, "E701", {"start": v(15.43, -54.28) * mm, "end": v(15.96, -54.52) * mm});
            skLineSegment(sketch, "E702", {"start": v(15.96, -54.52) * mm, "end": v(16.2, -54.55) * mm});
            skLineSegment(sketch, "E703", {"start": v(16.2, -54.55) * mm, "end": v(16.84, -53.2) * mm});
            skLineSegment(sketch, "E704", {"start": v(16.84, -53.2) * mm, "end": v(17.2, -51.96) * mm});
            skLineSegment(sketch, "E705", {"start": v(17.2, -51.96) * mm, "end": v(17.74, -51.1) * mm});
            skLineSegment(sketch, "E706", {"start": v(17.74, -51.1) * mm, "end": v(19.23, -49.7) * mm});
            skLineSegment(sketch, "E707", {"start": v(19.23, -49.7) * mm, "end": v(20.7, -48.74) * mm});
            skLineSegment(sketch, "E708", {"start": v(20.7, -48.74) * mm, "end": v(21.33, -47.9) * mm});
            skLineSegment(sketch, "E709", {"start": v(21.33, -47.9) * mm, "end": v(21.52, -46.29) * mm});
            skLineSegment(sketch, "E710", {"start": v(21.52, -46.29) * mm, "end": v(21.52, -45.14) * mm});
            skLineSegment(sketch, "E711", {"start": v(21.52, -45.14) * mm, "end": v(21.47, -44.46) * mm});
            skLineSegment(sketch, "E712", {"start": v(21.47, -44.46) * mm, "end": v(21.74, -43.75) * mm});
            skLineSegment(sketch, "E713", {"start": v(21.74, -43.75) * mm, "end": v(21.93, -42.95) * mm});
            skLineSegment(sketch, "E714", {"start": v(21.93, -42.95) * mm, "end": v(21.93, -39.6) * mm});
            skLineSegment(sketch, "E715", {"start": v(21.93, -39.6) * mm, "end": v(21.34, -36.45) * mm});
            skLineSegment(sketch, "E716", {"start": v(21.34, -36.45) * mm, "end": v(21.03, -35.16) * mm});
            skLineSegment(sketch, "E717", {"start": v(21.03, -35.16) * mm, "end": v(20.3, -34.22) * mm});
            skLineSegment(sketch, "E718", {"start": v(20.3, -34.22) * mm, "end": v(19.81, -33.74) * mm});
            skLineSegment(sketch, "E719", {"start": v(19.81, -33.74) * mm, "end": v(18.6, -33.47) * mm});
            skLineSegment(sketch, "E720", {"start": v(18.6, -33.47) * mm, "end": v(17.47, -33.34) * mm});
            skLineSegment(sketch, "E721", {"start": v(17.47, -33.34) * mm, "end": v(16.34, -33.42) * mm});
            skLineSegment(sketch, "E722", {"start": v(16.34, -33.42) * mm, "end": v(15.23, -33.62) * mm});
            skLineSegment(sketch, "E723", {"start": v(15.23, -33.62) * mm, "end": v(13.97, -34.3) * mm});
            skLineSegment(sketch, "E724", {"start": v(13.97, -34.3) * mm, "end": v(11.93, -35.5) * mm});
            skLineSegment(sketch, "E725", {"start": v(11.93, -35.5) * mm, "end": v(10.19, -36.27) * mm});
            skLineSegment(sketch, "E726", {"start": v(10.19, -36.27) * mm, "end": v(8.1, -37.05) * mm});
            skLineSegment(sketch, "E727", {"start": v(8.1, -37.05) * mm, "end": v(4.6, -37.54) * mm});
            skLineSegment(sketch, "E728", {"start": v(4.6, -37.54) * mm, "end": v(2.1, -37.56) * mm});
            skLineSegment(sketch, "E729", {"start": v(2.1, -37.56) * mm, "end": v(-0.37, -37.29) * mm});
            skLineSegment(sketch, "E730", {"start": v(-0.37, -37.29) * mm, "end": v(-2.78, -36.86) * mm});
            skLineSegment(sketch, "E731", {"start": v(-2.78, -36.86) * mm, "end": v(-4.46, -36.05) * mm});
            skLineSegment(sketch, "E732", {"start": v(-4.46, -36.05) * mm, "end": v(-5.42, -35.58) * mm});
            skLineSegment(sketch, "E733", {"start": v(-5.42, -35.58) * mm, "end": v(-6.02, -35.42) * mm});
            skLineSegment(sketch, "E734", {"start": v(-6.02, -35.42) * mm, "end": v(-6.53, -35.47) * mm});
            skLineSegment(sketch, "E735", {"start": v(-6.53, -35.47) * mm, "end": v(-7.92, -36.27) * mm});
            skLineSegment(sketch, "E736", {"start": v(-7.92, -36.27) * mm, "end": v(-11.71, -39.26) * mm});
            skLineSegment(sketch, "E737", {"start": v(-11.71, -39.26) * mm, "end": v(-14.65, -41.18) * mm});
            skLineSegment(sketch, "E738", {"start": v(-14.65, -41.18) * mm, "end": v(-18.68, -43.4) * mm});
            skLineSegment(sketch, "E739", {"start": v(-18.68, -43.4) * mm, "end": v(-21.9, -44.9) * mm});
            skSolve(sketch);
        }
        {
            var Q0;
            Q0=makeQuery(id+"F2.imprint","IMPRINT",FACE,{"disambiguationData":[TD([[makeQuery(id+"F2.imprint","IMPRINT",EDGE,{"derivedFrom":sQuery(id+"F2.wireOp",EDGE,"E10")}),1.0]])]});
            extrude(context, id + "F3", {"entities" : qUnion([Q0]), "operationType" : NewBodyOperationType.ADD, "depth" : 5 * mm, "offsetDistance" : 25 * mm});
        }
    });
